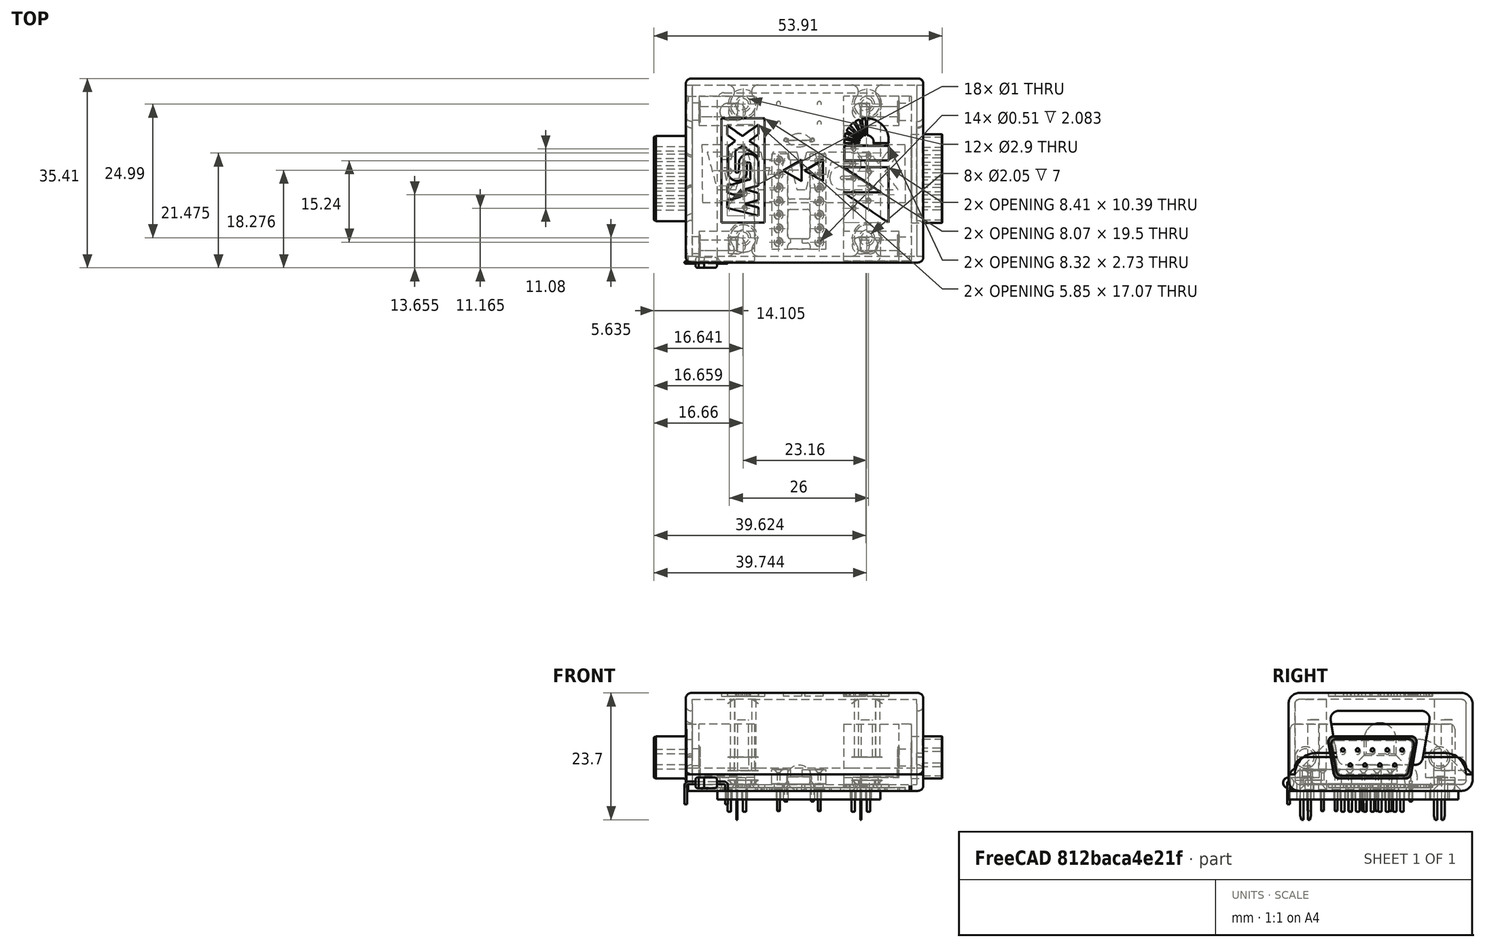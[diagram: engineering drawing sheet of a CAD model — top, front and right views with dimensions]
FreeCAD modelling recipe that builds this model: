
FCSTD DOCUMENT  (FreeCAD 0.19R)
Label: msx_mega_adapter_case
License: All rights reserved
LicenseURL: http://en.wikipedia.org/wiki/All_rights_reserved
objects: Sketcher::SketchObject×46, PartDesign::Pocket×19, PartDesign::Pad×11, Part::Feature×11, Part::Extrusion×9, Part::FeaturePython×9, App::Part×7, PartDesign::Fillet×6, PartDesign::Hole×6, PartDesign::LinearPattern×5, PartDesign::MultiTransform×3, PartDesign::Plane×3, PartDesign::Body×3, App::DocumentObjectGroup×3, Spreadsheet::Sheet×2, PartDesign::CoordinateSystem×1, App::Link×1
note: 174 computed .brp shape members not serialized (recipe doc carries the construction recipe); baked Part::Feature solids carry a one-line shape summary decoded from their .brp

FEATURE [Sketcher::SketchObject] Sketch  label="Initial sketch"
  FullyConstrained = true
  MapMode = 5
  Support = -> [XY_Plane001]
  expr: .Constraints.case_width = Spreadsheet.case_width
  expr: .Constraints.enclosure_length = Spreadsheet.case_length
  sketch-geometry (4):
    g0: LineSegment StartX=0 StartY=0 StartZ=0 EndX=44.4 EndY=0 EndZ=0
    g1: LineSegment StartX=44.4 StartY=0 StartZ=0 EndX=44.4 EndY=34.4 EndZ=0
    g2: LineSegment StartX=44.4 StartY=34.4 StartZ=0 EndX=0 EndY=34.4 EndZ=0
    g3: LineSegment StartX=0 StartY=34.4 StartZ=0 EndX=0 EndY=0 EndZ=0
  constraints (11):
    c: Coincident(g0,g1)
    c: Coincident(g1,g2)
    c: Coincident(g2,g3)
    c: Coincident(g3,g0)
    c: Horizontal(g0)
    c: Horizontal(g2)
    c: Vertical(g1)
    c: Vertical(g3)
    c: Coincident(g0,g-1)
    c: Distance(g2) = 44.4  'enclosure_length'
    c: Distance(g1) = 34.4  'case_width'
FEATURE [PartDesign::Pad] Pad  label="Initial Pad"
  Direction = (1,1,1)
  Length = 18.3
  Length2 = 100
  Profile = -> Sketch
  Type = 0
  expr: Length = Spreadsheet.case_heigth
FEATURE [Spreadsheet::Sheet] Spreadsheet
  cells = A1=Parameter description; B1=Parameter alias; C1=Value; A2=PCB - Length; B2=pcb_length; C2(pcb_length)=42; A3=PCB - Width; B3=pcb_width; C3(pcb_width)=31.6; A4=PCB - Thickness; B4=pcb_thickness; C4(pcb_thickness)=1.6; A5=PCB - Bottom clearance; B5=pcb_bottom_clearance; C5(pcb_bottom_clearance)=0.8; A6=PCB - Hole distance between connectors; B6=pcb_hole_dist_connectors; C6(pcb_hole_dist_connectors)=23.16; A7=Clearance between PCB and case; B7=clearance; C7(clearance)=0.2; A8=Connector clearance; B8=connector_clearance; C8(connector_clearance)=0.8; A9=Electronics heigth; B9=electronics_heigth; C9(electronics_heigth)=12.4; A10=Case - Wall thickness; B10=case_wall_thickness; C10(case_wall_thickness)=1.2; A11=Case - Upper clearance; B11=case_upper_clearance; C11(case_upper_clearance)=0.5; A12=Case - Top/Bottom thickness; B12=case_top_bottom_thickness; C12(case_top_bottom_thickness)=1.5; A13=Case - Length; B13=case_length; C13(case_length)==pcb_length + 2 * case_wall_thickness; A14=Case - Width; B14=case_width; C14(case_width)==pcb_width + 2 * (clearance + case_wall_thickness); A15=Case - Heigth; B15=case_heigth; C15(case_heigth)==2 * case_top_bottom_thickness + pcb_bottom_clearance + pcb_thickness + electronics_heigth + case_upper_clearance; A16=Case - External fillet; B16=case_external_fillet; C16(case_external_fillet)=2; A17=Case - Front and rear faces fillet; B17=case_front_rear_fillet; C17(case_front_rear_fillet)=1; A18=Case - DB9 hole center height; B18=case_db9_hole_center_height; C18(case_db9_hole_center_height)==case_wall_thickness + pcb_bottom_clearance + pcb_thickness + db9_screw_hole_heigth; A19=DB9 - Shield width (A); B19=db9_shield_width; C19(db9_shield_width)=30.84; A20=DB9 - Distance between screws (B); B20=db9_distance_screws; C20(db9_distance_screws)=24.99; A21=DB9 - Connector max width (C); B21=db9_connector_max_width; C21(db9_connector_max_width)=16.92; A22=DB9 - Connector max heigth; B22=db9_connector_max_heigth; C22(db9_connector_max_heigth)=8.5; A23=DB9 - Screw hole heigth; B23=db9_screw_hole_heigth; C23(db9_screw_hole_heigth)=6.3; A24=DB9 - Distance from bottom hole to front shield; B24=db9_bottom_hole_front_shield; C24(db9_bottom_hole_front_shield)==8.08 + 1.42; A25=DB9 - Connector angle; B25=db9_connector_angle; C25(db9_connector_angle)=10; A26=DB9 - Bottom distance between shield and connector; B26=db9_bottom_shield_connector; C26(db9_bottom_shield_connector)=1; A27=DB9 - Left side offset; B27=db9_left_side_offset; C27(db9_left_side_offset)=0.3; A28=DB9 - Right side offset; B28=db9_right_side_offset; C28(db9_right_side_offset)=0.65; A29=DB9 - Foot heigth; B29=db9_foot_heigth; C29(db9_foot_heigth)=2.5; A30=M3 - Non-threaded hole diameter; B30=m3_non_threaded_hole_diam; C30(m3_non_threaded_hole_diam)=2.5; A31=M3 - Non-threaded hole depth; B31=m3_non_threaded_hole_depth; C31(m3_non_threaded_hole_depth)==case_top_bottom_thickness + pcb_bottom_clearance; A32=M3 - Threaded hole depth; B32=m3_threaded_hole_depth; C32(m3_threaded_hole_depth)=7; A33=M3 - Pass-through hole; B33=m3_pass_through_hole_diam; C33(m3_pass_through_hole_diam)=3; A34=M3 - Pole radius; B34=m3_pole_radius; C34(m3_pole_radius)=2.4; A35=M3 - Castellated diameter; B35=m3_castellated_diameter; C35(m3_castellated_diameter)=5; A36=M3 - Castellated angle; B36=m3_castellated_angle; C36(m3_castellated_angle)=45; A37=Label - MSX width; B37=label_msx_width; C37(label_msx_width)=15; A38=Label - MSX heigth; B38=label_msx_heigth; C38(label_msx_heigth)=6.211; A39=Label - MSX horizontal position; B39=label_msx_hpos; C39(label_msx_hpos)==case_wall_thickness + db9_bottom_hole_front_shield; A40=Label - MSX vertical position; B40=label_msx_vpos; C40(label_msx_vpos)==case_width / 2; A41=Label - MD horizontal position; B41=label_md_hpos; C41(label_md_hpos)==case_length - (case_wall_thickness + db9_bottom_hole_front_shield); A42=Label - MD vertical position; B42=label_md_vpos; C42(label_md_vpos)==case_width / 2; A43=Cable - Stress relief diameter; B43=cable_stress_relief_diam; C43(cable_stress_relief_diam)=5.3; A44=Slice - Sides angle; B44=slice_sides_angle; C44(slice_sides_angle)=45
FEATURE [PartDesign::Fillet] Fillet  label="Case Fillet"
  Base = -> Pad [Edge9,Edge3,Edge10,Edge4]
  BaseFeature = -> Pad
  Radius = 2
  SupportTransform = false
  expr: Radius = Spreadsheet.case_external_fillet
FEATURE [PartDesign::CoordinateSystem] Local_CS_ead3
  AttacherType = Attacher::AttachEngine3D
  MapMode = 2
  Support = -> [X_Axis002]
FEATURE [Part::Feature] Pcb_ead3
  Placement = pos=(-110.3,90.8,0) rot=(0,0,1;0rad)
  shape: bbox 30.48 x 31.75 x 1.6 mm, 52 faces (baked)
FEATURE [Sketcher::SketchObject] PCB_Sketch_ead3
  FullyConstrained = false
  sketch-geometry (8):
    g0: LineSegment StartX=7.175 StartY=31.745 StartZ=0 EndX=35.115 EndY=31.745 EndZ=0
    g1: LineSegment StartX=5.905 StartY=1.265 StartZ=0 EndX=5.905 EndY=30.475 EndZ=0
    g2: LineSegment StartX=35.115 StartY=-0.005 StartZ=0 EndX=7.175 EndY=-0.005 EndZ=0
    g3: LineSegment StartX=36.385 StartY=30.475 StartZ=0 EndX=36.385 EndY=1.265 EndZ=0
    g4: ArcOfCircle CenterX=7.175 CenterY=1.265 CenterZ=0 NormalX=0 NormalY=0 NormalZ=-1 AngleXU=-1.5708 Radius=1.27 StartAngle=0 EndAngle=1.5708
    g5: ArcOfCircle CenterX=35.115 CenterY=1.265 CenterZ=0 NormalX=0 NormalY=0 NormalZ=-1 AngleXU=3.14159 Radius=1.27 StartAngle=0 EndAngle=1.5708
    g6: ArcOfCircle CenterX=7.175 CenterY=30.475 CenterZ=0 NormalX=0 NormalY=0 NormalZ=-1 AngleXU=-1.04279e-06 Radius=1.27 StartAngle=0 EndAngle=1.5708
    g7: ArcOfCircle CenterX=35.115 CenterY=30.475 CenterZ=0 NormalX=0 NormalY=0 NormalZ=-1 AngleXU=1.5708 Radius=1.27 StartAngle=0 EndAngle=1.5708
  constraints (8):
    c: Coincident(g1,g4)
    c: Coincident(g1,g6)
    c: Coincident(g2,g4)
    c: Coincident(g0,g6)
    c: Coincident(g2,g5)
    c: Coincident(g0,g7)
    c: Coincident(g3,g5)
    c: Coincident(g3,g7)
FEATURE [Part::Feature] Shape  label="J1_DSUB-9_Female_Horizontal_P2.77x2.84mm_EdgePinOffset7.70mm_Housed_
MountingHolesOffset9.12mm_00005d11216c"
  Placement = pos=(10.985,10.155,0) rot=(0,0,-1;1.5708rad)
  shape: bbox 18.74 x 30.96 x 17.98 mm, 179 faces (baked)
FEATURE [Part::Feature] Shape001  label="J2_DSUB-9_Male_Horizontal_P2.77x2.84mm_EdgePinOffset7.70mm_Housed_
MountingHolesOffset9.12mm_00005da618ed"
  Placement = pos=(31.305,10.155,0) rot=(0,0,1;1.5708rad)
  shape: bbox 18.44 x 30.96 x 17.98 mm, 181 faces (baked)
FEATURE [Part::Feature] Shape002  label="C1_C_Disc_D47mm_W25mm_P500mm_00005fced085"
  Placement = pos=(23.685,22.855,0) rot=(0,0,1;3.14159rad)
  shape: bbox 5.5 x 2.5 x 6.8 mm, 10 faces (baked)
FEATURE [Part::Feature] Shape003  label="U1_DIP_14_W762mm_Socket_00005fced0e1"
  Placement = pos=(17.335,19.045,0) rot=(0,0,1;0rad)
  shape: bbox 10.16 x 17.78 x 7.787 mm, 207 faces (baked)
FEATURE [Part::Feature] Part__Feature  label="D_DO-35_SOD27_P7.62mm_Horizontal"
  shape: bbox 8.244 x 0.5 x 4.312 mm, 7 faces (baked)
FEATURE [Part::Feature] Part__Feature001  label="D_DO-35_SOD27_P7.62mm_Horizontal001"
  shape: bbox 4 x 2.165 x 2.165 mm, 9 faces (baked)
FEATURE [App::Part] D_DO_35_SOD27_P7_62mm_Horizontal  label="D2_D_DO-35_SOD27_P7.62mm_Horizontal002_00005fced598"
  Group = -> [Part__Feature,Part__Feature001]
  Origin = -> Origin008
  Placement = pos=(24.955,26.03,0) rot=(0,0,1;3.14159rad)
FEATURE [App::Link] D2_D_DO_35_SOD27_P7_62mm_Horizontal002_00005fced598_ln_  label="D1_D_DO-35_SOD27_P7.62mm_Horizontal002_00005fcede50"
  LinkPlacement = pos=(24.955,29.713,0) rot=(0,0,1;3.14159rad)
  LinkedObject = -> D_DO_35_SOD27_P7_62mm_Horizontal
  Placement = pos=(24.955,29.713,0) rot=(0,0,1;3.14159rad)
FEATURE [App::Part] Top_ead3
  Group = -> [Shape,Shape001,Shape002,Shape003,D_DO_35_SOD27_P7_62mm_Horizontal,D2_D_DO_35_SOD27_P7_62mm_Horizontal002_00005fced598_ln_]
  Origin = -> Origin005
FEATURE [App::Part] Step_Models_ead3
  Group = -> [Top_ead3]
  Origin = -> Origin004
FEATURE [Part::Feature] pads_area006001  label="topPads_ead3"
  Placement = pos=(-110.3,90.8,0.02) rot=(0,0,1;0rad)
  shape: bbox 27.6 x 29.32 x 2e-07 mm, 42 faces, 0 solids (baked)
FEATURE [Part::Feature] Shape004001  label="topTracks_ead3"
  Placement = pos=(-110.3,90.8,0.01) rot=(0,0,1;0rad)
  shape: bbox 29.57 x 22.35 x 2e-07 mm, 11 faces, 0 solids (baked)
FEATURE [Part::Feature] pads_area006008001  label="botPads_ead3"
  Placement = pos=(-110.3,90.8,-1.62) rot=(0,0,1;0rad)
  shape: bbox 27.6 x 29.32 x 2e-07 mm, 42 faces, 0 solids (baked)
FEATURE [Part::Feature] zones_area001  label="botZones_ead3"
  Placement = pos=(-110.3,90.8,-1.61) rot=(0,0,1;0rad)
  shape: bbox 29.51 x 30.78 x 2e-07 mm, 1 faces, 0 solids (baked)
FEATURE [App::Part] Board_Geoms_ead3
  Group = -> [Pcb_ead3,PCB_Sketch_ead3,pads_area006001,Shape004001,pads_area006008001,zones_area001]
  Origin = -> Origin003
FEATURE [App::Part] Board_ead3  label="MSX Mega Adapter PCB"
  Group = -> [Local_CS_ead3,Board_Geoms_ead3,Step_Models_ead3]
  Origin = -> Origin002
  Placement = pos=(1.2,1.4,3.6) rot=(0,0,1;0rad)
  expr: .Placement.Base.x = Spreadsheet.case_wall_thickness
  expr: .Placement.Base.y = Spreadsheet.case_wall_thickness + Spreadsheet.clearance
  expr: .Placement.Base.z = Spreadsheet.case_wall_thickness + Spreadsheet.pcb_bottom_clearance + Spreadsheet.pcb_thickness
FEATURE [Sketcher::SketchObject] Sketch001  label="db9_male_hole"
  FullyConstrained = true
  MapMode = 5
  Placement = pos=(44.4,0,0) rot=(0.57735,0.57735,0.57735;2.0944rad)
  Support = -> [Fillet]
  expr: Constraints[11] = Spreadsheet.db9_connector_max_width / 2 + Spreadsheet.connector_clearance
  expr: Constraints[18] = Spreadsheet.db9_connector_max_heigth + 2 * Spreadsheet.connector_clearance
  expr: Constraints[19] = Spreadsheet.case_wall_thickness + Spreadsheet.clearance + Spreadsheet.db9_left_side_offset + Spreadsheet.db9_shield_width / 2
  expr: Constraints[28] = Spreadsheet.case_db9_hole_center_height
  sketch-geometry (12):
    g0: LineSegment StartX=9.36 StartY=14.95 StartZ=0 EndX=24.88 EndY=14.95 EndZ=0
    g1: LineSegment StartX=26.3572 StartY=13.1895 StartZ=0 EndX=25.1053 EndY=6.08953 EndZ=0
    g2: LineSegment StartX=23.6281 StartY=4.85 StartZ=0 EndX=10.6119 EndY=4.85 EndZ=0
    g3: LineSegment StartX=9.13471 StartY=6.08953 StartZ=0 EndX=7.88279 EndY=13.1895 EndZ=0
    g4: LineSegment StartX=17.12 StartY=14.95 StartZ=0 EndX=17.12 EndY=0 EndZ=0
    g5: ArcOfCircle CenterX=9.36 CenterY=13.45 CenterZ=0 NormalX=0 NormalY=0 NormalZ=1 AngleXU=0 Radius=1.5 StartAngle=1.5708 EndAngle=3.31613
    g6: ArcOfCircle CenterX=24.88 CenterY=13.45 CenterZ=0 NormalX=0 NormalY=0 NormalZ=1 AngleXU=0 Radius=1.5 StartAngle=6.10865 EndAngle=7.85398
    g7: ArcOfCircle CenterX=23.6281 CenterY=6.35 CenterZ=0 NormalX=0 NormalY=0 NormalZ=1 AngleXU=0 Radius=1.5 StartAngle=4.71239 EndAngle=6.10865
    g8: ArcOfCircle CenterX=10.6119 CenterY=6.35 CenterZ=0 NormalX=0 NormalY=0 NormalZ=1 AngleXU=0 Radius=1.5 StartAngle=3.31613 EndAngle=4.71239
    g9: LineSegment StartX=7.86 StartY=14.95 StartZ=0 EndX=7.86 EndY=4.85 EndZ=0
    g10: LineSegment StartX=26.38 StartY=14.95 StartZ=0 EndX=26.38 EndY=4.85 EndZ=0
    g11: GeomPoint X=7.86 Y=9.9 Z=0
  constraints (29):
    c: Horizontal(g0)
    c: PointOnObject(g4,g-1)
    c: Tangent(g0,g5) = 1.5708
    c: Tangent(g3,g5) = 1.5708
    c: Tangent(g0,g6) = 1.5708
    c: Tangent(g1,g6) = 1.5708
    c: Tangent(g1,g7) = 1.5708
    c: Tangent(g2,g7) = 1.5708
    c: Tangent(g2,g8) = 1.5708
    c: Tangent(g3,g8) = 1.5708
    c: Vertical(g9)
    c: Distance(g9,g4) = 9.26
    c: Vertical(g10)
    c: Tangent(g6,g10)
    c: Symmetric(g0,g0,g4)
    c: Symmetric(g2,g2,g4)
    c: Angle(g4,g3) = 0.174533
    c: Symmetric(g3,g1,g4)
    c: Distance(g2,g0) = 10.1
    c: Distance(g4,g-2) = 17.12
    c: Radius(g5) = 1.5
    c: Radius(g8) = 1.5
    c: Horizontal(g4,g9)
    c: Horizontal(g2,g10)
    c: Horizontal(g9,g2)
    c: PointOnObject(g9,g0)
    c: Symmetric(g10,g9,g4)
    c: Symmetric(g9,g9,g11)
    c: Distance(g11,g-1) = 9.9
FEATURE [PartDesign::Pocket] Pocket  label="DB9 Connector holes"
  BaseFeature = -> Fillet
  Length = 44.4
  Length2 = 100
  Profile = -> Sketch001
  Type = 0
  expr: Length = Spreadsheet.case_length
FEATURE [Sketcher::SketchObject] Sketch002  label="case_inner void"
  AttachmentOffset = pos=(0,0,1.2) rot=(0,0,1;0rad)
  ExternalGeometry = -> [Pocket]
  FullyConstrained = true
  MapMode = 5
  Placement = pos=(1.2,-3e-16,3e-16) rot=(0.57735,0.57735,0.57735;2.0944rad)
  Support = -> [YZ_Plane001]
  expr: .AttachmentOffset.Base.z = Spreadsheet.case_wall_thickness
  expr: Constraints[15] = Spreadsheet.case_wall_thickness
  expr: Constraints[16] = Spreadsheet.case_wall_thickness
  expr: Constraints[17] = Spreadsheet.case_wall_thickness
  expr: Constraints[18] = Spreadsheet.case_wall_thickness
  sketch-geometry (8):
    g0: LineSegment StartX=32.4 StartY=17.1 StartZ=0 EndX=2 EndY=17.1 EndZ=0
    g1: LineSegment StartX=1.2 StartY=16.3 StartZ=0 EndX=1.2 EndY=2 EndZ=0
    g2: LineSegment StartX=2 StartY=1.2 StartZ=0 EndX=32.4 EndY=1.2 EndZ=0
    g3: LineSegment StartX=33.2 StartY=2 StartZ=0 EndX=33.2 EndY=16.3 EndZ=0
    g4: ArcOfCircle CenterX=32.4 CenterY=16.3 CenterZ=0 NormalX=0 NormalY=0 NormalZ=1 AngleXU=0 Radius=0.8 StartAngle=3.4e-15 EndAngle=1.5708
    g5: ArcOfCircle CenterX=32.4 CenterY=2 CenterZ=0 NormalX=0 NormalY=0 NormalZ=1 AngleXU=0 Radius=0.8 StartAngle=4.71239 EndAngle=6.28319
    g6: ArcOfCircle CenterX=2 CenterY=2 CenterZ=0 NormalX=0 NormalY=0 NormalZ=1 AngleXU=0 Radius=0.8 StartAngle=3.14159 EndAngle=4.71239
    g7: ArcOfCircle CenterX=2 CenterY=16.3 CenterZ=0 NormalX=0 NormalY=0 NormalZ=1 AngleXU=0 Radius=0.8 StartAngle=1.5708 EndAngle=3.14159
  constraints (20):
    c: Tangent(g0,g4) = -1.5708
    c: Tangent(g3,g4) = -1.5708
    c: Tangent(g3,g5) = -1.5708
    c: Tangent(g2,g5) = -1.5708
    c: Tangent(g2,g6) = -1.5708
    c: Tangent(g1,g6) = -1.5708
    c: Tangent(g0,g7) = -1.5708
    c: Tangent(g1,g7) = -1.5708
    c: Horizontal(g0)
    c: Horizontal(g2)
    c: Vertical(g1)
    c: Vertical(g3)
    c: Equal(g7,g6)
    c: Equal(g6,g5)
    c: Equal(g5,g4)
    c: Distance(g0,g-3) = 1.2
    c: Distance(g3,g-5) = 1.2
    c: Distance(g1,g-9) = 1.2
    c: Distance(g2,g-7) = 1.2
    c: Vertical(g0,g-10)
FEATURE [PartDesign::Pocket] Pocket001  label="Case emptying"
  BaseFeature = -> Pocket
  Length = 42
  Length2 = 100
  Profile = -> Sketch002
  Reversed = true
  Type = 0
  expr: Length = Spreadsheet.case_length - 2 * Spreadsheet.case_wall_thickness
FEATURE [Sketcher::SketchObject] Sketch003  label="pcb_front_support_sketch"
  ExternalGeometry = -> [Pocket001]
  FullyConstrained = true
  MapMode = 5
  Placement = pos=(-3e-16,3e-16,1.2) rot=(0,0,1;0rad)
  Support = -> [Pocket001]
  expr: Constraints[10] = Spreadsheet.m3_pole_radius
  expr: Constraints[2] = Spreadsheet.db9_distance_screws / 2
  expr: Constraints[9] = Spreadsheet.m3_pass_through_hole_diam
  expr: Constraints[0] = Spreadsheet.case_wall_thickness + Spreadsheet.db9_bottom_hole_front_shield
  expr: Constraints[4] = Spreadsheet.case_wall_thickness + Spreadsheet.db9_bottom_hole_front_shield
  sketch-geometry (13):
    g0: ArcOfCircle CenterX=10.7 CenterY=4.625 CenterZ=0 NormalX=0 NormalY=0 NormalZ=1 AngleXU=0 Radius=2.4 StartAngle=5.60805 EndAngle=10.0999
    g1: LineSegment StartX=1.4e-15 StartY=17.12 StartZ=0 EndX=10.7 EndY=17.12 EndZ=0
    g2: ArcOfCircle CenterX=13.4982 CenterY=2.38462 CenterZ=0 NormalX=0 NormalY=0 NormalZ=1 AngleXU=0 Radius=1.18462 StartAngle=2.46646 EndAngle=4.71239
    g3: ArcOfCircle CenterX=7.90176 CenterY=2.38462 CenterZ=0 NormalX=0 NormalY=0 NormalZ=1 AngleXU=0 Radius=1.18462 StartAngle=4.71239 EndAngle=6.95832
    g4: Circle CenterX=10.7 CenterY=4.625 CenterZ=0 NormalX=0 NormalY=0 NormalZ=1 AngleXU=0 Radius=1.5
    g5: GeomPoint X=10.7 Y=3.125 Z=0
    g6: LineSegment StartX=7.90176 StartY=1.2 StartZ=0 EndX=13.4982 EndY=1.2 EndZ=0
    g7: GeomPoint X=10.7 Y=1.2 Z=0
    g8: LineSegment StartX=7.8249 StartY=33.2 StartZ=0 EndX=13.5751 EndY=33.2 EndZ=0
    g9: ArcOfCircle CenterX=7.8249 CenterY=31.9169 CenterZ=0 NormalX=0 NormalY=0 NormalZ=1 AngleXU=0 Radius=1.28308 StartAngle=5.60805 EndAngle=7.85398
    g10: ArcOfCircle CenterX=10.7 CenterY=29.615 CenterZ=0 NormalX=0 NormalY=0 NormalZ=1 AngleXU=0 Radius=2.4 StartAngle=2.46646 EndAngle=6.95832
    g11: ArcOfCircle CenterX=13.5751 CenterY=31.9169 CenterZ=0 NormalX=0 NormalY=0 NormalZ=1 AngleXU=0 Radius=1.28308 StartAngle=1.5708 EndAngle=3.81672
    g12: GeomPoint X=10.7 Y=33.2 Z=0
  constraints (31):
    c: Distance(g0,g-2) = 10.7
    c: Horizontal(g1)
    c: Distance(g0,g1) = 12.495
    c: Symmetric(g-3,g-3,g1)
    c: Distance(g1) = 10.7
    c: Equal(g3,g2)
    c: Tangent(g0,g2) = 1.5708
    c: Tangent(g0,g3) = 1.5708
    c: Coincident(g4,g0)
    c: Diameter(g4) = 3
    c: Radius(g0) = 2.4
    c: PointOnObject(g5,g4)
    c: Vertical(g5,g0)
    c: Horizontal(g5,g0)
    c: Horizontal(g0,g0)
    c: Coincident(g6,g3)
    c: Horizontal(g6)
    c: Symmetric(g3,g2,g7)
    c: PointOnObject(g3,g-4)
    c: Tangent(g6,g2) = -1.5708
    c: Equal(g9,g11)
    c: Tangent(g10,g11) = 1.5708
    c: Tangent(g10,g9) = 1.5708
    c: Coincident(g8,g9)
    c: Horizontal(g8)
    c: Tangent(g8,g11) = 1.5708
    c: Symmetric(g10,g0,g1)
    c: Symmetric(g0,g9,g1)
    c: PointOnObject(g8,g-5)
    c: Symmetric(g8,g8,g12)
    c: Vertical(g12,g10)
FEATURE [PartDesign::Pad] Pad001  label="PCB front support"
  BaseFeature = -> Pocket001
  Direction = (1,1,1)
  Length = 0.8
  Length2 = 100
  Profile = -> Sketch003
  Type = 2
  expr: Length = Spreadsheet.pcb_bottom_clearance
FEATURE [Sketcher::SketchObject] Sketch005  label="Bottom hole sketch"
  ExternalGeometry = -> [Pad001]
  FullyConstrained = true
  MapMode = 5
  Placement = pos=(0,0,0) rot=(1,0,0;3.14159rad)
  Support = -> [Pad001]
  expr: Constraints[0] = Spreadsheet.m3_pass_through_hole_diam
  sketch-geometry (2):
    g0: Circle CenterX=10.7 CenterY=-4.625 CenterZ=0 NormalX=0 NormalY=0 NormalZ=1 AngleXU=0 Radius=1.5
    g1: Circle CenterX=10.7 CenterY=-29.615 CenterZ=0 NormalX=0 NormalY=0 NormalZ=1 AngleXU=0 Radius=1.5
  constraints (4):
    c: Diameter(g0) = 3
    c: Coincident(g0,g-3)
    c: Coincident(g1,g-4)
    c: Equal(g1,g0)
FEATURE [PartDesign::LinearPattern] LinearPattern  label="Supports LinearPattern"
  Direction = -> X_Axis001
  Length = 23.16
  Occurrences = 2
  expr: Length = Spreadsheet.pcb_hole_dist_connectors
FEATURE [PartDesign::Hole] Hole  label="Bottom hole"
  BaseFeature = -> Pad001
  Depth = 2
  DepthType = 0
  Diameter = 2.9
  DrillForDepth = false
  DrillPoint = 0
  DrillPointAngle = 118
  HoleCutCountersinkAngle = 90
  HoleCutCustomValues = false
  HoleCutDepth = 1.2
  HoleCutDiameter = 5.5
  HoleCutType = 2
  ModelActualThread = false
  Profile = -> Sketch005
  Tapered = false
  TaperedAngle = 90
  ThreadAngle = 60
  ThreadClass = 0
  ThreadCutOffInner = 0.0487139
  ThreadCutOffOuter = 0.0974279
  ThreadDirection = 0
  ThreadFit = 0
  ThreadPitch = 0.45
  ThreadSize = 8
  ThreadType = 1
  Threaded = false
  expr: HoleCutDepth = Spreadsheet.case_wall_thickness
  expr: Depth = Spreadsheet.case_wall_thickness + Spreadsheet.pcb_bottom_clearance
FEATURE [Sketcher::SketchObject] Sketch006  label="Middle cut sketch"
  ExternalGeometry = -> [Hole,Sketch003]
  FullyConstrained = true
  MapMode = 5
  Placement = pos=(0,0,2) rot=(1,0,0;3.14159rad)
  Support = -> [Hole]
  sketch-geometry (8):
    g0: ArcOfCircle CenterX=10.7 CenterY=-4.625 CenterZ=0 NormalX=0 NormalY=0 NormalZ=1 AngleXU=0 Radius=2.4 StartAngle=3.25303 EndAngle=6.17175
    g1: LineSegment StartX=8.31489 StartY=-4.8919 StartZ=0 EndX=7.90176 EndY=-1.2 EndZ=0
    g2: LineSegment StartX=13.0851 StartY=-4.8919 StartZ=0 EndX=13.4982 EndY=-1.2 EndZ=0
    g3: ArcOfCircle CenterX=10.7 CenterY=-29.615 CenterZ=0 NormalX=0 NormalY=0 NormalZ=1 AngleXU=0 Radius=2.4 StartAngle=0.126458 EndAngle=3.01514
    g4: LineSegment StartX=8.31916 StartY=-29.3123 StartZ=0 EndX=7.8249 EndY=-33.2 EndZ=0
    g5: LineSegment StartX=13.0808 StartY=-29.3123 StartZ=0 EndX=13.5751 EndY=-33.2 EndZ=0
    g6: LineSegment StartX=7.8249 StartY=-33.2 StartZ=0 EndX=13.5751 EndY=-33.2 EndZ=0
    g7: LineSegment StartX=7.90176 StartY=-1.2 StartZ=0 EndX=13.4982 EndY=-1.2 EndZ=0
  constraints (16):
    c: Tangent(g0,g2) = -1.5708
    c: Tangent(g1,g0) = 1.5708
    c: Coincident(g5,g6)
    c: Coincident(g4,g6)
    c: Coincident(g2,g7)
    c: Coincident(g1,g7)
    c: Coincident(g3,g-5)
    c: PointOnObject(g3,g-5)
    c: Coincident(g0,g-6)
    c: Coincident(g1,g-8)
    c: Coincident(g2,g-8)
    c: PointOnObject(g0,g-6)
    c: Coincident(g4,g-7)
    c: Tangent(g3,g4) = -1.5708
    c: Tangent(g5,g3) = 1.5708
    c: Coincident(g5,g-7)
FEATURE [PartDesign::Pocket] Pocket002  label="Middle cut for pcb and DB9 foot"
  BaseFeature = -> Hole
  Length = 4.3
  Length2 = 100
  Profile = -> Sketch006
  Type = 0
  expr: Length = Spreadsheet.db9_foot_heigth + Spreadsheet.pcb_thickness + Spreadsheet.clearance
FEATURE [Sketcher::SketchObject] Sketch007  label="M3 threaded sketch"
  ExternalGeometry = -> [Pocket002]
  FullyConstrained = true
  MapMode = 5
  Placement = pos=(0,0,6.3) rot=(1,0,0;3.14159rad)
  Support = -> [Pocket002]
  sketch-geometry (3):
    g0: Circle CenterX=10.7 CenterY=-4.625 CenterZ=0 NormalX=0 NormalY=0 NormalZ=1 AngleXU=0 Radius=0.5
    g1: LineSegment StartX=0 StartY=-17.12 StartZ=0 EndX=10.7 EndY=-17.12 EndZ=0
    g2: Circle CenterX=10.7 CenterY=-29.615 CenterZ=0 NormalX=0 NormalY=0 NormalZ=1 AngleXU=0 Radius=0.5
  constraints (7):
    c: Diameter(g0) = 1
    c: Horizontal(g1)
    c: Symmetric(g-3,g-3,g1)
    c: Vertical(g1,g0)
    c: Equal(g0,g2)
    c: Symmetric(g0,g2,g1)
    c: Coincident(g2,g-4)
FEATURE [PartDesign::Hole] Hole001  label="M3 threaded hole"
  BaseFeature = -> Pocket002
  Depth = 7
  DepthType = 0
  Diameter = 2.05
  DrillForDepth = false
  DrillPoint = 0
  DrillPointAngle = 118
  HoleCutCountersinkAngle = 90
  HoleCutCustomValues = false
  HoleCutDepth = 0
  HoleCutDiameter = 6.1
  HoleCutType = 0
  ModelActualThread = false
  Profile = -> Sketch007
  Tapered = false
  TaperedAngle = 90
  ThreadAngle = 60
  ThreadClass = 0
  ThreadCutOffInner = 0.0487139
  ThreadCutOffOuter = 0.0974279
  ThreadDirection = 0
  ThreadFit = 0
  ThreadPitch = 0.45
  ThreadSize = 8
  ThreadType = 1
  Threaded = true
  expr: Depth = Spreadsheet.m3_threaded_hole_depth
FEATURE [PartDesign::MultiTransform] MultiTransform  label="Supports replication"
  BaseFeature = -> Hole001
  Originals = -> [Pad001,Hole,Pocket002,Hole001]
  Transformations = -> [LinearPattern]
FEATURE [Sketcher::SketchObject] Sketch008  label="Split wire left"
  ExternalGeometry = -> [MultiTransform]
  FullyConstrained = true
  MapMode = 5
  Placement = pos=(0,0,0) rot=(0.57735,-0.57735,-0.57735;2.0944rad)
  Support = -> [MultiTransform]
  expr: Constraints[11] = Spreadsheet.case_external_fillet
  expr: Constraints[5] = Spreadsheet.case_top_bottom_thickness + Spreadsheet.pcb_bottom_clearance + Spreadsheet.pcb_thickness / 2
  expr: Constraints[14] = Spreadsheet.case_wall_thickness
  sketch-geometry (5):
    g0: LineSegment StartX=-33.2 StartY=4.3 StartZ=0 EndX=-34.4 EndY=3.1 EndZ=0
    g1: LineSegment StartX=-1.2 StartY=4.3 StartZ=0 EndX=0 EndY=3.1 EndZ=0
    g2: LineSegment StartX=-31.2 StartY=6.3 StartZ=0 EndX=-3.2 EndY=6.3 EndZ=0
    g3: ArcOfCircle CenterX=-31.2 CenterY=4.3 CenterZ=0 NormalX=0 NormalY=0 NormalZ=1 AngleXU=0 Radius=2 StartAngle=1.5708 EndAngle=3.14159
    g4: ArcOfCircle CenterX=-3.2 CenterY=4.3 CenterZ=0 NormalX=0 NormalY=0 NormalZ=1 AngleXU=0 Radius=2 StartAngle=0 EndAngle=1.5708
  constraints (16):
    c: PointOnObject(g0,g-3)
    c: Angle(g0,g-3) = 0.785398
    c: PointOnObject(g1,g-2)
    c: Horizontal(g0,g1)
    c: Horizontal(g1,g0)
    c: Distance(g-1,g1) = 3.1
    c: Horizontal(g2)
    c: Equal(g1,g0)
    c: Tangent(g2,g3) = 1.5708
    c: Tangent(g2,g4) = 1.5708
    c: Equal(g3,g4)
    c: Radius(g3) = 2
    c: Coincident(g1,g4)
    c: Coincident(g0,g3)
    c: Distance(g0,g-3) = 1.2
    c: Horizontal(g3,g0)
FEATURE [Sketcher::SketchObject] Sketch010  label="Split wire right"
  ExternalGeometry = -> [MultiTransform]
  FullyConstrained = true
  MapMode = 5
  Placement = pos=(44.4,0,0) rot=(0.57735,0.57735,0.57735;2.0944rad)
  Support = -> [MultiTransform]
  expr: Constraints[11] = Spreadsheet.case_external_fillet
  expr: Constraints[4] = Sketch008.Constraints[5]
  expr: Constraints[14] = Spreadsheet.case_wall_thickness
  sketch-geometry (5):
    g0: LineSegment StartX=33.2 StartY=4.3 StartZ=0 EndX=34.4 EndY=3.1 EndZ=0
    g1: LineSegment StartX=1.2 StartY=4.3 StartZ=0 EndX=0 EndY=3.1 EndZ=0
    g2: LineSegment StartX=31.2 StartY=6.3 StartZ=0 EndX=3.2 EndY=6.3 EndZ=0
    g3: ArcOfCircle CenterX=3.2 CenterY=4.3 CenterZ=0 NormalX=0 NormalY=0 NormalZ=1 AngleXU=0 Radius=2 StartAngle=1.5708 EndAngle=3.14159
    g4: ArcOfCircle CenterX=31.2 CenterY=4.3 CenterZ=0 NormalX=0 NormalY=0 NormalZ=1 AngleXU=0 Radius=2 StartAngle=0 EndAngle=1.5708
  constraints (16):
    c: PointOnObject(g0,g-3)
    c: PointOnObject(g1,g-2)
    c: Horizontal(g0,g1)
    c: Horizontal(g1,g0)
    c: Distance(g-1,g1) = 3.1
    c: Horizontal(g2)
    c: Equal(g1,g0)
    c: Angle(g-3,g0) = 0.785398
    c: Tangent(g2,g3) = -1.5708
    c: Tangent(g2,g4) = -1.5708
    c: Equal(g3,g4)
    c: Radius(g3) = 2
    c: Coincident(g1,g3)
    c: Coincident(g4,g0)
    c: Distance(g0,g-3) = 1.2
    c: Horizontal(g1,g3)
FEATURE [Sketcher::SketchObject] Sketch011  label="Split wire sides"
  ExternalGeometry = -> [Sketch008]
  FullyConstrained = true
  MapMode = 5
  Placement = pos=(0,0,0) rot=(0.57735,-0.57735,-0.57735;2.0944rad)
  Support = -> [MultiTransform]
  sketch-geometry (2):
    g0: LineSegment StartX=-34.4 StartY=3.1 StartZ=0 EndX=-33.2 EndY=4.3 EndZ=0
    g1: LineSegment StartX=0 StartY=3.1 StartZ=0 EndX=-1.2 EndY=4.3 EndZ=0
  constraints (4):
    c: Coincident(g0,g-3)
    c: Coincident(g0,g-4)
    c: Coincident(g1,g-6)
    c: Coincident(g1,g-5)
FEATURE [Part::Extrusion] Extrude  label="Split plane left"
  Base = -> Sketch008
  Dir = (-1,0,0)
  DirMode = 2
  FaceMakerClass = Part::FaceMakerBullseye
  LengthFwd = 1.2
  LengthRev = 0
  Reversed = true
  Solid = false
  Symmetric = false
  expr: LengthFwd = Spreadsheet.case_wall_thickness
FEATURE [Part::Extrusion] Extrude001  label="Split plane sides"
  Base = -> Sketch011
  Dir = (-1,0,0)
  DirMode = 2
  FaceMakerClass = Part::FaceMakerBullseye
  LengthFwd = 44.4
  LengthRev = 0
  Reversed = true
  Solid = false
  Symmetric = false
  expr: LengthFwd = Spreadsheet.case_length
FEATURE [Part::Extrusion] Extrude002  label="Split plane right"
  Base = -> Sketch010
  Dir = (1,0,0)
  DirMode = 2
  FaceMakerClass = Part::FaceMakerBullseye
  LengthFwd = 1.2
  LengthRev = 0
  Reversed = true
  Solid = false
  Symmetric = false
FEATURE [PartDesign::Plane] DatumPlane  label="Top Plane"
  AttachmentOffset = pos=(0,0,18.3) rot=(0,0,1;0rad)
  Length = 60
  MapMode = 5
  Placement = pos=(0,0,18.3) rot=(0,0,1;0rad)
  ResizeMode = 0
  Support = -> [XY_Plane001]
  Width = 60
  expr: .AttachmentOffset.Base.z = Spreadsheet.case_heigth
FEATURE [Sketcher::SketchObject] Sketch015  label="Arrows logo"
  FullyConstrained = true
  MapMode = 5
  Placement = pos=(0,0,18.3) rot=(0,0,1;0rad)
  Support = -> [DatumPlane]
  expr: Constraints[16] = Spreadsheet.case_length / 2
  expr: Constraints[15] = Spreadsheet.case_width / 2
  sketch-geometry (6):
    g0: LineSegment StartX=21.6641 StartY=19.2 StartZ=0 EndX=18.2 EndY=17.2 EndZ=0
    g1: LineSegment StartX=18.2 StartY=17.2 StartZ=0 EndX=21.6641 EndY=15.2 EndZ=0
    g2: LineSegment StartX=21.6641 StartY=15.2 StartZ=0 EndX=21.6641 EndY=19.2 EndZ=0
    g3: LineSegment StartX=25.6641 StartY=19.2 StartZ=0 EndX=22.2 EndY=17.2 EndZ=0
    g4: LineSegment StartX=22.2 StartY=17.2 StartZ=0 EndX=25.6641 EndY=15.2 EndZ=0
    g5: LineSegment StartX=25.6641 StartY=15.2 StartZ=0 EndX=25.6641 EndY=19.2 EndZ=0
  constraints (18):
    c: Coincident(g1,g0)
    c: Coincident(g2,g1)
    c: Coincident(g2,g0)
    c: Vertical(g2)
    c: Angle(g2,g1) = 1.0472
    c: Angle(g1,g0) = 1.0472
    c: Coincident(g4,g3)
    c: Coincident(g5,g4)
    c: Coincident(g5,g3)
    c: Vertical(g5)
    c: Angle(g5,g4) = 1.0472
    c: Angle(g4,g3) = 1.0472
    c: Horizontal(g1,g4)
    c: Horizontal(g3,g0)
    c: Distance(g0,g5) = 4
    c: Distance(g0,g-1) = 17.2
    c: Distance(g3,g-2) = 22.2
    c: Distance(g5) = 4
FEATURE [Sketcher::SketchObject] Sketch016  label="MSX Logo"
  AttachmentOffset = pos=(10.7,17.2,0) rot=(0,0,1;1.5708rad)
  FullyConstrained = false
  MapMode = 5
  Placement = pos=(10.7,17.2,18.3) rot=(0,0,1;1.5708rad)
  Support = -> [DatumPlane]
  expr: .AttachmentOffset.Base.x = Spreadsheet.label_msx_hpos
  expr: .AttachmentOffset.Base.y = Spreadsheet.label_msx_vpos
  sketch-geometry (39):
    g0: BSplineCurve PolesCount=2 KnotsCount=2 Degree=1 IsPeriodic=0
    g1: BSplineCurve PolesCount=2 KnotsCount=2 Degree=1 IsPeriodic=0
    g2: BSplineCurve PolesCount=2 KnotsCount=2 Degree=1 IsPeriodic=0
    g3: BSplineCurve PolesCount=2 KnotsCount=2 Degree=1 IsPeriodic=0
    g4: BSplineCurve PolesCount=2 KnotsCount=2 Degree=1 IsPeriodic=0
    g5: BSplineCurve PolesCount=2 KnotsCount=2 Degree=1 IsPeriodic=0
    g6: BSplineCurve PolesCount=2 KnotsCount=2 Degree=1 IsPeriodic=0
    g7: BSplineCurve PolesCount=2 KnotsCount=2 Degree=1 IsPeriodic=0
    g8: BSplineCurve PolesCount=2 KnotsCount=2 Degree=1 IsPeriodic=0
    g9: BSplineCurve PolesCount=2 KnotsCount=2 Degree=1 IsPeriodic=0
    g10: BSplineCurve PolesCount=4 KnotsCount=2 Degree=3 IsPeriodic=0
    g11: BSplineCurve PolesCount=2 KnotsCount=2 Degree=1 IsPeriodic=0
    g12: BSplineCurve PolesCount=4 KnotsCount=2 Degree=3 IsPeriodic=0
    g13: BSplineCurve PolesCount=4 KnotsCount=2 Degree=3 IsPeriodic=0
    g14: BSplineCurve PolesCount=2 KnotsCount=2 Degree=1 IsPeriodic=0
    g15: BSplineCurve PolesCount=2 KnotsCount=2 Degree=1 IsPeriodic=0
    g16: BSplineCurve PolesCount=2 KnotsCount=2 Degree=1 IsPeriodic=0
    g17: BSplineCurve PolesCount=2 KnotsCount=2 Degree=1 IsPeriodic=0
    g18: BSplineCurve PolesCount=2 KnotsCount=2 Degree=1 IsPeriodic=0
    g19: BSplineCurve PolesCount=2 KnotsCount=2 Degree=1 IsPeriodic=0
    g20: BSplineCurve PolesCount=2 KnotsCount=2 Degree=1 IsPeriodic=0
    g21: BSplineCurve PolesCount=2 KnotsCount=2 Degree=1 IsPeriodic=0
    g22: BSplineCurve PolesCount=2 KnotsCount=2 Degree=1 IsPeriodic=0
    g23: BSplineCurve PolesCount=2 KnotsCount=2 Degree=1 IsPeriodic=0
    g24: BSplineCurve PolesCount=2 KnotsCount=2 Degree=1 IsPeriodic=0
    g25: BSplineCurve PolesCount=2 KnotsCount=2 Degree=1 IsPeriodic=0
    g26: BSplineCurve PolesCount=2 KnotsCount=2 Degree=1 IsPeriodic=0
    g27: BSplineCurve PolesCount=4 KnotsCount=2 Degree=3 IsPeriodic=0
    g28: BSplineCurve PolesCount=2 KnotsCount=2 Degree=1 IsPeriodic=0
    g29: BSplineCurve PolesCount=4 KnotsCount=2 Degree=3 IsPeriodic=0
    g30: BSplineCurve PolesCount=4 KnotsCount=2 Degree=3 IsPeriodic=0
    g31: BSplineCurve PolesCount=2 KnotsCount=2 Degree=1 IsPeriodic=0
    g32: BSplineCurve PolesCount=2 KnotsCount=2 Degree=1 IsPeriodic=0
    g33: BSplineCurve PolesCount=2 KnotsCount=2 Degree=1 IsPeriodic=0
    g34: BSplineCurve PolesCount=2 KnotsCount=2 Degree=1 IsPeriodic=0
    g35: BSplineCurve PolesCount=2 KnotsCount=2 Degree=1 IsPeriodic=0
    g36: BSplineCurve PolesCount=2 KnotsCount=2 Degree=1 IsPeriodic=0
    g37: BSplineCurve PolesCount=2 KnotsCount=2 Degree=1 IsPeriodic=0
    g38: BSplineCurve PolesCount=2 KnotsCount=2 Degree=1 IsPeriodic=0
  constraints (39):
    c: Coincident(g0,g1)
    c: Coincident(g1,g2)
    c: Coincident(g2,g3)
    c: Coincident(g3,g0)
    c: Coincident(g4,g5)
    c: Coincident(g5,g6)
    c: Coincident(g6,g7)
    c: Coincident(g7,g8)
    c: Coincident(g8,g9)
    c: Coincident(g9,g10)
    c: Coincident(g10,g11)
    c: Coincident(g11,g12)
    c: Coincident(g12,g13)
    c: Coincident(g13,g14)
    c: Coincident(g14,g15)
    c: Coincident(g15,g16)
    c: Coincident(g16,g17)
    c: Coincident(g17,g18)
    c: Coincident(g18,g19)
    c: Coincident(g19,g20)
    c: Coincident(g20,g21)
    c: Coincident(g21,g22)
    c: Coincident(g22,g23)
    c: Coincident(g23,g24)
    c: Coincident(g24,g25)
    c: Coincident(g25,g26)
    c: Coincident(g26,g27)
    c: Coincident(g27,g28)
    c: Coincident(g28,g29)
    c: Coincident(g29,g30)
    c: Coincident(g30,g31)
    c: Coincident(g31,g32)
    c: Coincident(g32,g33)
    c: Coincident(g33,g34)
    c: Coincident(g34,g35)
    c: Coincident(g35,g36)
    c: Coincident(g36,g37)
    c: Coincident(g37,g38)
    c: Coincident(g38,g4)
FEATURE [PartDesign::Pocket] Pocket003  label="MSX Logo pocket"
  BaseFeature = -> MultiTransform
  Length = 0.6
  Length2 = 100
  Profile = -> Sketch016
  Type = 0
  expr: Length = Spreadsheet.case_wall_thickness / 2
FEATURE [PartDesign::Pocket] Pocket004  label="Arrows Logo pocket"
  BaseFeature = -> Pocket003
  Length = 0.6
  Length2 = 100
  Profile = -> Sketch015
  Type = 0
  expr: Length = Spreadsheet.case_wall_thickness / 2
FEATURE [Sketcher::SketchObject] Sketch017  label="MD Logo"
  AttachmentOffset = pos=(33.7,17.2,0) rot=(0,0,1;1.5708rad)
  FullyConstrained = false
  MapMode = 5
  Placement = pos=(33.7,17.2,18.3) rot=(0,0,1;1.5708rad)
  Support = -> [Pocket004,DatumPlane]
  expr: .AttachmentOffset.Base.x = Spreadsheet.label_md_hpos
  expr: .AttachmentOffset.Base.y = Spreadsheet.label_md_vpos
  sketch-geometry (50):
    g0: BSplineCurve PolesCount=2 KnotsCount=2 Degree=1 IsPeriodic=0
    g1: BSplineCurve PolesCount=2 KnotsCount=2 Degree=1 IsPeriodic=0
    g2: BSplineCurve PolesCount=2 KnotsCount=2 Degree=1 IsPeriodic=0
    g3: BSplineCurve PolesCount=2 KnotsCount=2 Degree=1 IsPeriodic=0
    g4: BSplineCurve PolesCount=2 KnotsCount=2 Degree=1 IsPeriodic=0
    g5: BSplineCurve PolesCount=2 KnotsCount=2 Degree=1 IsPeriodic=0
    g6: BSplineCurve PolesCount=2 KnotsCount=2 Degree=1 IsPeriodic=0
    g7: BSplineCurve PolesCount=2 KnotsCount=2 Degree=1 IsPeriodic=0
    g8: BSplineCurve PolesCount=2 KnotsCount=2 Degree=1 IsPeriodic=0
    g9: BSplineCurve PolesCount=2 KnotsCount=2 Degree=1 IsPeriodic=0
    g10: BSplineCurve PolesCount=2 KnotsCount=2 Degree=1 IsPeriodic=0
    g11: BSplineCurve PolesCount=2 KnotsCount=2 Degree=1 IsPeriodic=0
    g12: BSplineCurve PolesCount=4 KnotsCount=2 Degree=3 IsPeriodic=0
    g13: BSplineCurve PolesCount=2 KnotsCount=2 Degree=1 IsPeriodic=0
    g14: BSplineCurve PolesCount=4 KnotsCount=2 Degree=3 IsPeriodic=0
    g15: BSplineCurve PolesCount=2 KnotsCount=2 Degree=1 IsPeriodic=0
    g16: BSplineCurve PolesCount=4 KnotsCount=2 Degree=3 IsPeriodic=0
    g17: BSplineCurve PolesCount=4 KnotsCount=2 Degree=3 IsPeriodic=0
    g18: BSplineCurve PolesCount=2 KnotsCount=2 Degree=1 IsPeriodic=0
    g19: BSplineCurve PolesCount=2 KnotsCount=2 Degree=1 IsPeriodic=0
    g20: BSplineCurve PolesCount=4 KnotsCount=2 Degree=3 IsPeriodic=0
    g21: BSplineCurve PolesCount=2 KnotsCount=2 Degree=1 IsPeriodic=0
    g22: BSplineCurve PolesCount=4 KnotsCount=2 Degree=3 IsPeriodic=0
    g23: BSplineCurve PolesCount=2 KnotsCount=2 Degree=1 IsPeriodic=0
    g24: BSplineCurve PolesCount=4 KnotsCount=2 Degree=3 IsPeriodic=0
    g25: BSplineCurve PolesCount=2 KnotsCount=2 Degree=1 IsPeriodic=0
    g26: BSplineCurve PolesCount=4 KnotsCount=2 Degree=3 IsPeriodic=0
    g27: BSplineCurve PolesCount=2 KnotsCount=2 Degree=1 IsPeriodic=0
    g28: BSplineCurve PolesCount=4 KnotsCount=2 Degree=3 IsPeriodic=0
    g29: BSplineCurve PolesCount=2 KnotsCount=2 Degree=1 IsPeriodic=0
    g30: BSplineCurve PolesCount=4 KnotsCount=2 Degree=3 IsPeriodic=0
    g31: BSplineCurve PolesCount=2 KnotsCount=2 Degree=1 IsPeriodic=0
    g32: BSplineCurve PolesCount=2 KnotsCount=2 Degree=1 IsPeriodic=0
    g33: BSplineCurve PolesCount=4 KnotsCount=2 Degree=3 IsPeriodic=0
    g34: BSplineCurve PolesCount=2 KnotsCount=2 Degree=1 IsPeriodic=0
    g35: BSplineCurve PolesCount=4 KnotsCount=2 Degree=3 IsPeriodic=0
    g36: BSplineCurve PolesCount=2 KnotsCount=2 Degree=1 IsPeriodic=0
    g37: BSplineCurve PolesCount=2 KnotsCount=2 Degree=1 IsPeriodic=0
    g38: BSplineCurve PolesCount=4 KnotsCount=2 Degree=3 IsPeriodic=0
    g39: BSplineCurve PolesCount=2 KnotsCount=2 Degree=1 IsPeriodic=0
    g40: BSplineCurve PolesCount=4 KnotsCount=2 Degree=3 IsPeriodic=0
    g41: BSplineCurve PolesCount=2 KnotsCount=2 Degree=1 IsPeriodic=0
    g42: BSplineCurve PolesCount=4 KnotsCount=2 Degree=3 IsPeriodic=0
    g43: BSplineCurve PolesCount=4 KnotsCount=2 Degree=3 IsPeriodic=0
    g44: BSplineCurve PolesCount=2 KnotsCount=2 Degree=1 IsPeriodic=0
    g45: BSplineCurve PolesCount=4 KnotsCount=2 Degree=3 IsPeriodic=0
    g46: BSplineCurve PolesCount=2 KnotsCount=2 Degree=1 IsPeriodic=0
    g47: BSplineCurve PolesCount=4 KnotsCount=2 Degree=3 IsPeriodic=0
    g48: BSplineCurve PolesCount=4 KnotsCount=2 Degree=3 IsPeriodic=0
    g49: BSplineCurve PolesCount=2 KnotsCount=2 Degree=1 IsPeriodic=0
  constraints (50):
    c: Coincident(g0,g1)
    c: Coincident(g1,g2)
    c: Coincident(g2,g3)
    c: Coincident(g3,g4)
    c: Coincident(g4,g5)
    c: Coincident(g5,g6)
    c: Coincident(g6,g0)
    c: Coincident(g7,g8)
    c: Coincident(g8,g9)
    c: Coincident(g9,g10)
    c: Coincident(g10,g7)
    c: Coincident(g11,g12)
    c: Coincident(g12,g13)
    c: Coincident(g13,g14)
    c: Coincident(g14,g15)
    c: Coincident(g15,g16)
    c: Coincident(g16,g17)
    c: Coincident(g17,g18)
    c: Coincident(g18,g11)
    c: Coincident(g19,g20)
    c: Coincident(g20,g21)
    c: Coincident(g21,g22)
    c: Coincident(g22,g19)
    c: Coincident(g23,g24)
    c: Coincident(g24,g25)
    c: Coincident(g25,g26)
    c: Coincident(g26,g23)
    c: Coincident(g27,g28)
    c: Coincident(g28,g29)
    c: Coincident(g29,g30)
    c: Coincident(g30,g31)
    c: Coincident(g31,g27)
    c: Coincident(g32,g33)
    c: Coincident(g33,g34)
    c: Coincident(g34,g35)
    c: Coincident(g35,g36)
    c: Coincident(g36,g32)
    c: Coincident(g37,g38)
    c: Coincident(g38,g39)
    c: Coincident(g39,g40)
    c: Coincident(g40,g41)
    c: Coincident(g41,g37)
    c: Coincident(g42,g43)
    c: Coincident(g43,g44)
    c: Coincident(g44,g45)
    c: Coincident(g45,g46)
    c: Coincident(g46,g47)
    c: Coincident(g47,g48)
    c: Coincident(g48,g49)
    c: Coincident(g49,g42)
FEATURE [PartDesign::Pocket] Pocket005  label="MD Logo pocket"
  BaseFeature = -> Pocket004
  Length = 0.6
  Length2 = 100
  Profile = -> Sketch017
  Type = 0
  expr: Length = Spreadsheet.case_wall_thickness / 2
FEATURE [PartDesign::LinearPattern] LinearPattern001
  BaseFeature = -> Pocket005
  Direction = -> Sketch016 [N_Axis]
  Length = 17.1
  Occurrences = 2
  Originals = -> [Pocket003,Pocket004,Pocket005]
  Reversed = true
  expr: Length = Spreadsheet.case_heigth - Spreadsheet.case_wall_thickness
FEATURE [PartDesign::Fillet] Fillet001  label="Fillet last operation"
  Base = -> LinearPattern001 [Face5,Face2]
  BaseFeature = -> LinearPattern001
  Radius = 1
  SupportTransform = false
  expr: Radius = Spreadsheet.case_front_rear_fillet
FEATURE [PartDesign::Body] Body  label="case"
  Group = -> [DatumPlane,Sketch,Pad,Fillet,Sketch001,Pocket,Sketch002,Pocket001,Sketch003,Pad001,Sketch005,Hole,Pocket002,Hole001,Sketch007,Sketch006,MultiTransform,Pocket003,LinearPattern,Sketch016,Pocket004,Pocket005,Sketch015,Sketch017,LinearPattern001,Fillet001,Sketch008,Sketch011,Sketch010]
  Origin = -> Origin001
  Tip = -> Fillet001
FEATURE [App::Part] Part  label="MSX Mega Adapter Case"
  Group = -> [Body]
  Origin = -> Origin
FEATURE [Part::FeaturePython] Slice  # WARN: FeaturePython — macro-defined, semantics opaque (R4)
  Base = -> Body
  Mode = 1
  Tolerance = 0
  Tools = -> [Extrude,Extrude001,Extrude002]
FEATURE [Part::FeaturePython] Slice_child0  label="Bottom"  # WARN: FeaturePython — macro-defined, semantics opaque (R4)
  Base = -> Slice
  FilterType = 1
  Invert = false
  OverrideMaxVal = 0
  WindowFrom = 80
  WindowTo = 100
  items = 0
FEATURE [Part::FeaturePython] Slice_child1  label="Top"  # WARN: FeaturePython — macro-defined, semantics opaque (R4)
  Base = -> Slice
  FilterType = 1
  Invert = false
  OverrideMaxVal = 0
  WindowFrom = 80
  WindowTo = 100
  items = 1
FEATURE [App::DocumentObjectGroup] GrExplode_Slice  label="MSX-Mega Adapter Slice"
  Group = -> [Slice_child0,Slice_child1]
FEATURE [Sketcher::SketchObject] Sketch018  label="Initial sketch001"
  FullyConstrained = true
  MapMode = 5
  Support = -> [XY_Plane010]
  expr: .Constraints.enclosure_length = Spreadsheet.case_length
  expr: .Constraints.case_width = Spreadsheet.case_width
  sketch-geometry (4):
    g0: LineSegment StartX=0 StartY=0 StartZ=0 EndX=44.4 EndY=0 EndZ=0
    g1: LineSegment StartX=44.4 StartY=0 StartZ=0 EndX=44.4 EndY=34.4 EndZ=0
    g2: LineSegment StartX=44.4 StartY=34.4 StartZ=0 EndX=0 EndY=34.4 EndZ=0
    g3: LineSegment StartX=0 StartY=34.4 StartZ=0 EndX=0 EndY=0 EndZ=0
  constraints (11):
    c: Coincident(g0,g1)
    c: Coincident(g1,g2)
    c: Coincident(g2,g3)
    c: Coincident(g3,g0)
    c: Horizontal(g0)
    c: Horizontal(g2)
    c: Vertical(g1)
    c: Vertical(g3)
    c: Coincident(g0,g-1)
    c: Distance(g2) = 44.4  'enclosure_length'
    c: Distance(g1) = 34.4  'case_width'
FEATURE [PartDesign::Pad] Pad002  label="Initial Pad001"
  Direction = (1,1,1)
  Length = 18.3
  Length2 = 100
  Profile = -> Sketch018
  Type = 0
  expr: Length = Spreadsheet.case_heigth
FEATURE [PartDesign::Fillet] Fillet002  label="Case Fillet001"
  Base = -> Pad002 [Edge9,Edge3,Edge10,Edge4]
  BaseFeature = -> Pad002
  Radius = 2
  SupportTransform = false
  expr: Radius = Spreadsheet.case_external_fillet
FEATURE [Sketcher::SketchObject] Sketch019  label="db9_male_hole001"
  FullyConstrained = true
  MapMode = 5
  Placement = pos=(44.4,0,0) rot=(0.57735,0.57735,0.57735;2.0944rad)
  Support = -> [Fillet002]
  expr: Constraints[28] = Spreadsheet.case_db9_hole_center_height
  expr: Constraints[19] = Spreadsheet.case_wall_thickness + Spreadsheet.clearance + Spreadsheet.db9_left_side_offset + Spreadsheet.db9_shield_width / 2
  expr: Constraints[18] = Spreadsheet.db9_connector_max_heigth + 2 * Spreadsheet.connector_clearance
  expr: Constraints[11] = Spreadsheet.db9_connector_max_width / 2 + Spreadsheet.connector_clearance
  sketch-geometry (12):
    g0: LineSegment StartX=9.36 StartY=14.95 StartZ=0 EndX=24.88 EndY=14.95 EndZ=0
    g1: LineSegment StartX=26.3572 StartY=13.1895 StartZ=0 EndX=25.1053 EndY=6.08953 EndZ=0
    g2: LineSegment StartX=23.6281 StartY=4.85 StartZ=0 EndX=10.6119 EndY=4.85 EndZ=0
    g3: LineSegment StartX=9.13471 StartY=6.08953 StartZ=0 EndX=7.88279 EndY=13.1895 EndZ=0
    g4: LineSegment StartX=17.12 StartY=14.95 StartZ=0 EndX=17.12 EndY=0 EndZ=0
    g5: ArcOfCircle CenterX=9.36 CenterY=13.45 CenterZ=0 NormalX=0 NormalY=0 NormalZ=1 AngleXU=0 Radius=1.5 StartAngle=1.5708 EndAngle=3.31613
    g6: ArcOfCircle CenterX=24.88 CenterY=13.45 CenterZ=0 NormalX=0 NormalY=0 NormalZ=1 AngleXU=0 Radius=1.5 StartAngle=6.10865 EndAngle=7.85398
    g7: ArcOfCircle CenterX=23.6281 CenterY=6.35 CenterZ=0 NormalX=0 NormalY=0 NormalZ=1 AngleXU=0 Radius=1.5 StartAngle=4.71239 EndAngle=6.10865
    g8: ArcOfCircle CenterX=10.6119 CenterY=6.35 CenterZ=0 NormalX=0 NormalY=0 NormalZ=1 AngleXU=0 Radius=1.5 StartAngle=3.31613 EndAngle=4.71239
    g9: LineSegment StartX=7.86 StartY=14.95 StartZ=0 EndX=7.86 EndY=4.85 EndZ=0
    g10: LineSegment StartX=26.38 StartY=14.95 StartZ=0 EndX=26.38 EndY=4.85 EndZ=0
    g11: GeomPoint X=7.86 Y=9.9 Z=0
  constraints (29):
    c: Horizontal(g0)
    c: PointOnObject(g4,g-1)
    c: Tangent(g0,g5) = 1.5708
    c: Tangent(g3,g5) = 1.5708
    c: Tangent(g0,g6) = 1.5708
    c: Tangent(g1,g6) = 1.5708
    c: Tangent(g1,g7) = 1.5708
    c: Tangent(g2,g7) = 1.5708
    c: Tangent(g2,g8) = 1.5708
    c: Tangent(g3,g8) = 1.5708
    c: Vertical(g9)
    c: Distance(g9,g4) = 9.26
    c: Vertical(g10)
    c: Tangent(g6,g10)
    c: Symmetric(g0,g0,g4)
    c: Symmetric(g2,g2,g4)
    c: Angle(g4,g3) = 0.174533
    c: Symmetric(g3,g1,g4)
    c: Distance(g2,g0) = 10.1
    c: Distance(g4,g-2) = 17.12
    c: Radius(g5) = 1.5
    c: Radius(g8) = 1.5
    c: Horizontal(g4,g9)
    c: Horizontal(g2,g10)
    c: Horizontal(g9,g2)
    c: PointOnObject(g9,g0)
    c: Symmetric(g10,g9,g4)
    c: Symmetric(g9,g9,g11)
    c: Distance(g11,g-1) = 9.9
FEATURE [PartDesign::Pocket] Pocket006  label="DB9 Connector holes001"
  BaseFeature = -> Fillet002
  Length = 44.4
  Length2 = 100
  Profile = -> Sketch019
  Type = 0
  expr: Length = Spreadsheet.case_length
FEATURE [Sketcher::SketchObject] Sketch020  label="case_inner void001"
  AttachmentOffset = pos=(0,0,1.2) rot=(0,0,1;0rad)
  ExternalGeometry = -> [Pocket006]
  FullyConstrained = true
  MapMode = 5
  Placement = pos=(1.2,-3e-16,3e-16) rot=(0.57735,0.57735,0.57735;2.0944rad)
  Support = -> [YZ_Plane010]
  expr: Constraints[18] = Spreadsheet.case_wall_thickness
  expr: Constraints[17] = Spreadsheet.case_wall_thickness
  expr: Constraints[16] = Spreadsheet.case_wall_thickness
  expr: Constraints[15] = Spreadsheet.case_wall_thickness
  expr: .AttachmentOffset.Base.z = Spreadsheet.case_wall_thickness
  sketch-geometry (8):
    g0: LineSegment StartX=32.4 StartY=17.1 StartZ=0 EndX=2 EndY=17.1 EndZ=0
    g1: LineSegment StartX=1.2 StartY=16.3 StartZ=0 EndX=1.2 EndY=2 EndZ=0
    g2: LineSegment StartX=2 StartY=1.2 StartZ=0 EndX=32.4 EndY=1.2 EndZ=0
    g3: LineSegment StartX=33.2 StartY=2 StartZ=0 EndX=33.2 EndY=16.3 EndZ=0
    g4: ArcOfCircle CenterX=32.4 CenterY=16.3 CenterZ=0 NormalX=0 NormalY=0 NormalZ=1 AngleXU=0 Radius=0.8 StartAngle=3.4e-15 EndAngle=1.5708
    g5: ArcOfCircle CenterX=32.4 CenterY=2 CenterZ=0 NormalX=0 NormalY=0 NormalZ=1 AngleXU=0 Radius=0.8 StartAngle=4.71239 EndAngle=6.28319
    g6: ArcOfCircle CenterX=2 CenterY=2 CenterZ=0 NormalX=0 NormalY=0 NormalZ=1 AngleXU=0 Radius=0.8 StartAngle=3.14159 EndAngle=4.71239
    g7: ArcOfCircle CenterX=2 CenterY=16.3 CenterZ=0 NormalX=0 NormalY=0 NormalZ=1 AngleXU=0 Radius=0.8 StartAngle=1.5708 EndAngle=3.14159
  constraints (20):
    c: Tangent(g0,g4) = -1.5708
    c: Tangent(g3,g4) = -1.5708
    c: Tangent(g3,g5) = -1.5708
    c: Tangent(g2,g5) = -1.5708
    c: Tangent(g2,g6) = -1.5708
    c: Tangent(g1,g6) = -1.5708
    c: Tangent(g0,g7) = -1.5708
    c: Tangent(g1,g7) = -1.5708
    c: Horizontal(g0)
    c: Horizontal(g2)
    c: Vertical(g1)
    c: Vertical(g3)
    c: Equal(g7,g6)
    c: Equal(g6,g5)
    c: Equal(g5,g4)
    c: Distance(g0,g-3) = 1.2
    c: Distance(g3,g-5) = 1.2
    c: Distance(g1,g-9) = 1.2
    c: Distance(g2,g-7) = 1.2
    c: Vertical(g0,g-10)
FEATURE [PartDesign::Pocket] Pocket007  label="Case emptying001"
  BaseFeature = -> Pocket006
  Length = 42
  Length2 = 100
  Profile = -> Sketch020
  Reversed = true
  Type = 0
  expr: Length = Spreadsheet.case_length - 2 * Spreadsheet.case_wall_thickness
FEATURE [Sketcher::SketchObject] Sketch021  label="pcb_front_support_sketch001"
  ExternalGeometry = -> [Pocket007]
  FullyConstrained = true
  MapMode = 5
  Placement = pos=(-3e-16,3e-16,1.2) rot=(0,0,1;0rad)
  Support = -> [Pocket007]
  expr: Constraints[4] = Spreadsheet.case_wall_thickness + Spreadsheet.db9_bottom_hole_front_shield
  expr: Constraints[0] = Spreadsheet.case_wall_thickness + Spreadsheet.db9_bottom_hole_front_shield
  expr: Constraints[9] = Spreadsheet.m3_pass_through_hole_diam
  expr: Constraints[2] = Spreadsheet.db9_distance_screws / 2
  expr: Constraints[10] = Spreadsheet.m3_pole_radius
  sketch-geometry (13):
    g0: ArcOfCircle CenterX=10.7 CenterY=4.625 CenterZ=0 NormalX=0 NormalY=0 NormalZ=1 AngleXU=0 Radius=2.4 StartAngle=5.60805 EndAngle=10.0999
    g1: LineSegment StartX=1.4e-15 StartY=17.12 StartZ=0 EndX=10.7 EndY=17.12 EndZ=0
    g2: ArcOfCircle CenterX=13.4982 CenterY=2.38462 CenterZ=0 NormalX=0 NormalY=0 NormalZ=1 AngleXU=0 Radius=1.18462 StartAngle=2.46646 EndAngle=4.71239
    g3: ArcOfCircle CenterX=7.90176 CenterY=2.38462 CenterZ=0 NormalX=0 NormalY=0 NormalZ=1 AngleXU=0 Radius=1.18462 StartAngle=4.71239 EndAngle=6.95832
    g4: Circle CenterX=10.7 CenterY=4.625 CenterZ=0 NormalX=0 NormalY=0 NormalZ=1 AngleXU=0 Radius=1.5
    g5: GeomPoint X=10.7 Y=3.125 Z=0
    g6: LineSegment StartX=7.90176 StartY=1.2 StartZ=0 EndX=13.4982 EndY=1.2 EndZ=0
    g7: GeomPoint X=10.7 Y=1.2 Z=0
    g8: LineSegment StartX=7.8249 StartY=33.2 StartZ=0 EndX=13.5751 EndY=33.2 EndZ=0
    g9: ArcOfCircle CenterX=7.8249 CenterY=31.9169 CenterZ=0 NormalX=0 NormalY=0 NormalZ=1 AngleXU=0 Radius=1.28308 StartAngle=5.60805 EndAngle=7.85398
    g10: ArcOfCircle CenterX=10.7 CenterY=29.615 CenterZ=0 NormalX=0 NormalY=0 NormalZ=1 AngleXU=0 Radius=2.4 StartAngle=2.46646 EndAngle=6.95832
    g11: ArcOfCircle CenterX=13.5751 CenterY=31.9169 CenterZ=0 NormalX=0 NormalY=0 NormalZ=1 AngleXU=0 Radius=1.28308 StartAngle=1.5708 EndAngle=3.81672
    g12: GeomPoint X=10.7 Y=33.2 Z=0
  constraints (31):
    c: Distance(g0,g-2) = 10.7
    c: Horizontal(g1)
    c: Distance(g0,g1) = 12.495
    c: Symmetric(g-3,g-3,g1)
    c: Distance(g1) = 10.7
    c: Equal(g3,g2)
    c: Tangent(g0,g2) = 1.5708
    c: Tangent(g0,g3) = 1.5708
    c: Coincident(g4,g0)
    c: Diameter(g4) = 3
    c: Radius(g0) = 2.4
    c: PointOnObject(g5,g4)
    c: Vertical(g5,g0)
    c: Horizontal(g5,g0)
    c: Horizontal(g0,g0)
    c: Coincident(g6,g3)
    c: Horizontal(g6)
    c: Symmetric(g3,g2,g7)
    c: PointOnObject(g3,g-4)
    c: Tangent(g6,g2) = -1.5708
    c: Equal(g9,g11)
    c: Tangent(g10,g11) = 1.5708
    c: Tangent(g10,g9) = 1.5708
    c: Coincident(g8,g9)
    c: Horizontal(g8)
    c: Tangent(g8,g11) = 1.5708
    c: Symmetric(g10,g0,g1)
    c: Symmetric(g0,g9,g1)
    c: PointOnObject(g8,g-5)
    c: Symmetric(g8,g8,g12)
    c: Vertical(g12,g10)
FEATURE [PartDesign::Pad] Pad003  label="PCB front support001"
  BaseFeature = -> Pocket007
  Direction = (1,1,1)
  Length = 0.8
  Length2 = 100
  Profile = -> Sketch021
  Type = 2
  expr: Length = Spreadsheet.pcb_bottom_clearance
FEATURE [Sketcher::SketchObject] Sketch022  label="Bottom hole sketch001"
  ExternalGeometry = -> [Pad003]
  FullyConstrained = true
  MapMode = 5
  Placement = pos=(0,0,0) rot=(1,0,0;3.14159rad)
  Support = -> [Pad003]
  expr: Constraints[0] = Spreadsheet.m3_pass_through_hole_diam
  sketch-geometry (2):
    g0: Circle CenterX=10.7 CenterY=-4.625 CenterZ=0 NormalX=0 NormalY=0 NormalZ=1 AngleXU=0 Radius=1.5
    g1: Circle CenterX=10.7 CenterY=-29.615 CenterZ=0 NormalX=0 NormalY=0 NormalZ=1 AngleXU=0 Radius=1.5
  constraints (4):
    c: Diameter(g0) = 3
    c: Coincident(g0,g-3)
    c: Coincident(g1,g-4)
    c: Equal(g1,g0)
FEATURE [PartDesign::LinearPattern] LinearPattern002  label="Supports LinearPattern001"
  Direction = -> X_Axis010
  Length = 23.16
  Occurrences = 2
  expr: Length = Spreadsheet.pcb_hole_dist_connectors
FEATURE [Sketcher::SketchObject] Sketch026  label="Split wire right001"
  AttachmentOffset = pos=(0,0,44.4) rot=(0,0,1;0rad)
  FullyConstrained = true
  MapMode = 5
  Placement = pos=(44.4,-9.9e-15,9.9e-15) rot=(0.57735,0.57735,0.57735;2.0944rad)
  Support = -> [YZ_Plane010]
  expr: .AttachmentOffset.Base.x = 0
  expr: .AttachmentOffset.Base.z = Spreadsheet.case_length
  expr: Constraints[2] = Spreadsheet.case_width
  expr: Constraints[10] = <<Spreadsheet>>.case_wall_thickness
  expr: Constraints[11] = Spreadsheet.case_top_bottom_thickness + Spreadsheet.pcb_thickness
  expr: Constraints[14] = Spreadsheet.case_external_fillet * 2
  sketch-geometry (5):
    g0: LineSegment StartX=33.2 StartY=3.1 StartZ=0 EndX=34.4 EndY=3.1 EndZ=0
    g1: LineSegment StartX=1.2 StartY=3.1 StartZ=0 EndX=0 EndY=3.1 EndZ=0
    g2: LineSegment StartX=29.2 StartY=7.1 StartZ=0 EndX=5.2 EndY=7.1 EndZ=0
    g3: ArcOfCircle CenterX=5.2 CenterY=3.1 CenterZ=0 NormalX=0 NormalY=0 NormalZ=1 AngleXU=0 Radius=4 StartAngle=1.5708 EndAngle=3.14159
    g4: ArcOfCircle CenterX=29.2 CenterY=3.1 CenterZ=0 NormalX=0 NormalY=0 NormalZ=1 AngleXU=0 Radius=4 StartAngle=0 EndAngle=1.5708
  constraints (16):
    c: Coincident(g1,g3)
    c: Coincident(g4,g0)
    c: Distance(g0,g-2) = 34.4
    c: Horizontal(g3,g4)
    c: Horizontal(g1,g3)
    c: Horizontal(g2)
    c: Tangent(g2,g3) = -1.5708
    c: Tangent(g4,g2) = -1.5708
    c: Horizontal(g0,g4)
    c: PointOnObject(g1,g-2)
    c: Distance(g1,g-2) = 1.2
    c: Distance(g1,g-1) = 3.1
    c: Horizontal(g0,g1)
    c: Equal(g0,g1)
    c: Radius(g3) = 4
    c: Horizontal(g1)
FEATURE [Sketcher::SketchObject] Sketch027  label="Split wire sides001"
  ExternalGeometry = -> [Sketch026]
  FullyConstrained = true
  MapMode = 5
  Placement = pos=(0,0,0) rot=(0.57735,0.57735,0.57735;2.0944rad)
  Support = -> [YZ_Plane010]
  sketch-geometry (2):
    g0: LineSegment StartX=0 StartY=3.1 StartZ=0 EndX=1.2 EndY=3.1 EndZ=0
    g1: LineSegment StartX=33.2 StartY=3.1 StartZ=0 EndX=34.4 EndY=3.1 EndZ=0
  constraints (4):
    c: Coincident(g0,g-4)
    c: Coincident(g0,g-4)
    c: Coincident(g1,g-3)
    c: Coincident(g1,g-3)
FEATURE [PartDesign::Hole] Hole003  label="Bottom hole001"
  BaseFeature = -> Pad003
  Depth = 2
  DepthType = 0
  Diameter = 2.9
  DrillForDepth = false
  DrillPoint = 0
  DrillPointAngle = 118
  HoleCutCountersinkAngle = 90
  HoleCutCustomValues = false
  HoleCutDepth = 1.2
  HoleCutDiameter = 5.5
  HoleCutType = 2
  ModelActualThread = false
  Profile = -> Sketch022
  Tapered = false
  TaperedAngle = 90
  ThreadAngle = 60
  ThreadClass = 0
  ThreadCutOffInner = 0.0487139
  ThreadCutOffOuter = 0.0974279
  ThreadDirection = 0
  ThreadFit = 0
  ThreadPitch = 0.45
  ThreadSize = 8
  ThreadType = 1
  Threaded = false
  expr: Depth = Spreadsheet.case_wall_thickness + Spreadsheet.pcb_bottom_clearance
  expr: HoleCutDepth = Spreadsheet.case_wall_thickness
FEATURE [Sketcher::SketchObject] Sketch023  label="Middle cut sketch001"
  ExternalGeometry = -> [Hole003,Sketch021]
  FullyConstrained = true
  MapMode = 5
  Placement = pos=(0,0,2) rot=(1,0,0;3.14159rad)
  Support = -> [Hole003]
  sketch-geometry (8):
    g0: ArcOfCircle CenterX=10.7 CenterY=-4.625 CenterZ=0 NormalX=0 NormalY=0 NormalZ=1 AngleXU=0 Radius=2.4 StartAngle=3.25303 EndAngle=6.17175
    g1: LineSegment StartX=8.31489 StartY=-4.8919 StartZ=0 EndX=7.90176 EndY=-1.2 EndZ=0
    g2: LineSegment StartX=13.0851 StartY=-4.8919 StartZ=0 EndX=13.4982 EndY=-1.2 EndZ=0
    g3: ArcOfCircle CenterX=10.7 CenterY=-29.615 CenterZ=0 NormalX=0 NormalY=0 NormalZ=1 AngleXU=0 Radius=2.4 StartAngle=0.126458 EndAngle=3.01514
    g4: LineSegment StartX=8.31916 StartY=-29.3123 StartZ=0 EndX=7.8249 EndY=-33.2 EndZ=0
    g5: LineSegment StartX=13.0808 StartY=-29.3123 StartZ=0 EndX=13.5751 EndY=-33.2 EndZ=0
    g6: LineSegment StartX=7.8249 StartY=-33.2 StartZ=0 EndX=13.5751 EndY=-33.2 EndZ=0
    g7: LineSegment StartX=7.90176 StartY=-1.2 StartZ=0 EndX=13.4982 EndY=-1.2 EndZ=0
  constraints (16):
    c: Tangent(g0,g2) = -1.5708
    c: Tangent(g1,g0) = 1.5708
    c: Coincident(g5,g6)
    c: Coincident(g4,g6)
    c: Coincident(g2,g7)
    c: Coincident(g1,g7)
    c: Coincident(g3,g-5)
    c: PointOnObject(g3,g-5)
    c: Coincident(g0,g-6)
    c: Coincident(g1,g-8)
    c: Coincident(g2,g-8)
    c: PointOnObject(g0,g-6)
    c: Coincident(g4,g-7)
    c: Tangent(g3,g4) = -1.5708
    c: Tangent(g5,g3) = 1.5708
    c: Coincident(g5,g-7)
FEATURE [PartDesign::Pocket] Pocket008  label="Middle cut for pcb and DB9 foot001"
  BaseFeature = -> Hole003
  Length = 4.3
  Length2 = 100
  Profile = -> Sketch023
  Type = 0
  expr: Length = Spreadsheet.db9_foot_heigth + Spreadsheet.pcb_thickness + Spreadsheet.clearance
FEATURE [Sketcher::SketchObject] Sketch024  label="M3 threaded sketch001"
  ExternalGeometry = -> [Pocket008]
  FullyConstrained = true
  MapMode = 5
  Placement = pos=(0,0,6.3) rot=(1,0,0;3.14159rad)
  Support = -> [Pocket008]
  sketch-geometry (3):
    g0: Circle CenterX=10.7 CenterY=-4.625 CenterZ=0 NormalX=0 NormalY=0 NormalZ=1 AngleXU=0 Radius=0.5
    g1: LineSegment StartX=0 StartY=-17.12 StartZ=0 EndX=10.7 EndY=-17.12 EndZ=0
    g2: Circle CenterX=10.7 CenterY=-29.615 CenterZ=0 NormalX=0 NormalY=0 NormalZ=1 AngleXU=0 Radius=0.5
  constraints (7):
    c: Diameter(g0) = 1
    c: Horizontal(g1)
    c: Symmetric(g-3,g-3,g1)
    c: Vertical(g1,g0)
    c: Equal(g0,g2)
    c: Symmetric(g0,g2,g1)
    c: Coincident(g2,g-4)
FEATURE [PartDesign::Hole] Hole002  label="M3 threaded hole001"
  BaseFeature = -> Pocket008
  Depth = 7
  DepthType = 0
  Diameter = 2.05
  DrillForDepth = false
  DrillPoint = 0
  DrillPointAngle = 118
  HoleCutCountersinkAngle = 90
  HoleCutCustomValues = false
  HoleCutDepth = 0
  HoleCutDiameter = 6.1
  HoleCutType = 0
  ModelActualThread = false
  Profile = -> Sketch024
  Tapered = false
  TaperedAngle = 90
  ThreadAngle = 60
  ThreadClass = 0
  ThreadCutOffInner = 0.0487139
  ThreadCutOffOuter = 0.0974279
  ThreadDirection = 0
  ThreadFit = 0
  ThreadPitch = 0.45
  ThreadSize = 8
  ThreadType = 1
  Threaded = true
  expr: Depth = Spreadsheet.m3_threaded_hole_depth
FEATURE [PartDesign::MultiTransform] MultiTransform001  label="Supports replication001"
  BaseFeature = -> Hole002
  Originals = -> [Pad003,Hole003,Pocket008,Hole002]
  Transformations = -> [LinearPattern002]
FEATURE [PartDesign::Plane] DatumPlane001  label="Top Plane001"
  AttachmentOffset = pos=(0,0,18.3) rot=(0,0,1;0rad)
  Length = 82.2411
  MapMode = 5
  Placement = pos=(0,0,18.3) rot=(0,0,1;0rad)
  ResizeMode = 0
  Support = -> [XY_Plane010]
  Width = 72.2411
  expr: .AttachmentOffset.Base.z = Spreadsheet.case_heigth
FEATURE [Sketcher::SketchObject] Sketch028  label="Arrows logo001"
  FullyConstrained = true
  MapMode = 5
  Placement = pos=(0,0,18.3) rot=(0,0,1;0rad)
  Support = -> [DatumPlane001]
  expr: Constraints[15] = Spreadsheet.case_width / 2
  expr: Constraints[16] = Spreadsheet.case_length / 2
  sketch-geometry (6):
    g0: LineSegment StartX=21.6641 StartY=19.2 StartZ=0 EndX=18.2 EndY=17.2 EndZ=0
    g1: LineSegment StartX=18.2 StartY=17.2 StartZ=0 EndX=21.6641 EndY=15.2 EndZ=0
    g2: LineSegment StartX=21.6641 StartY=15.2 StartZ=0 EndX=21.6641 EndY=19.2 EndZ=0
    g3: LineSegment StartX=25.6641 StartY=19.2 StartZ=0 EndX=22.2 EndY=17.2 EndZ=0
    g4: LineSegment StartX=22.2 StartY=17.2 StartZ=0 EndX=25.6641 EndY=15.2 EndZ=0
    g5: LineSegment StartX=25.6641 StartY=15.2 StartZ=0 EndX=25.6641 EndY=19.2 EndZ=0
  constraints (18):
    c: Coincident(g1,g0)
    c: Coincident(g2,g1)
    c: Coincident(g2,g0)
    c: Vertical(g2)
    c: Angle(g2,g1) = 1.0472
    c: Angle(g1,g0) = 1.0472
    c: Coincident(g4,g3)
    c: Coincident(g5,g4)
    c: Coincident(g5,g3)
    c: Vertical(g5)
    c: Angle(g5,g4) = 1.0472
    c: Angle(g4,g3) = 1.0472
    c: Horizontal(g1,g4)
    c: Horizontal(g3,g0)
    c: Distance(g0,g5) = 4
    c: Distance(g0,g-1) = 17.2
    c: Distance(g3,g-2) = 22.2
    c: Distance(g5) = 4
FEATURE [Sketcher::SketchObject] Sketch029  label="MSX Logo001"
  AttachmentOffset = pos=(10.7,17.2,0) rot=(0,0,1;1.5708rad)
  FullyConstrained = false
  MapMode = 5
  Placement = pos=(10.7,17.2,18.3) rot=(0,0,1;1.5708rad)
  Support = -> [DatumPlane001]
  expr: .AttachmentOffset.Base.y = Spreadsheet.label_msx_vpos
  expr: .AttachmentOffset.Base.x = Spreadsheet.label_msx_hpos
  sketch-geometry (39):
    g0: BSplineCurve PolesCount=2 KnotsCount=2 Degree=1 IsPeriodic=0
    g1: BSplineCurve PolesCount=2 KnotsCount=2 Degree=1 IsPeriodic=0
    g2: BSplineCurve PolesCount=2 KnotsCount=2 Degree=1 IsPeriodic=0
    g3: BSplineCurve PolesCount=2 KnotsCount=2 Degree=1 IsPeriodic=0
    g4: BSplineCurve PolesCount=2 KnotsCount=2 Degree=1 IsPeriodic=0
    g5: BSplineCurve PolesCount=2 KnotsCount=2 Degree=1 IsPeriodic=0
    g6: BSplineCurve PolesCount=2 KnotsCount=2 Degree=1 IsPeriodic=0
    g7: BSplineCurve PolesCount=2 KnotsCount=2 Degree=1 IsPeriodic=0
    g8: BSplineCurve PolesCount=2 KnotsCount=2 Degree=1 IsPeriodic=0
    g9: BSplineCurve PolesCount=2 KnotsCount=2 Degree=1 IsPeriodic=0
    g10: BSplineCurve PolesCount=4 KnotsCount=2 Degree=3 IsPeriodic=0
    g11: BSplineCurve PolesCount=2 KnotsCount=2 Degree=1 IsPeriodic=0
    g12: BSplineCurve PolesCount=4 KnotsCount=2 Degree=3 IsPeriodic=0
    g13: BSplineCurve PolesCount=4 KnotsCount=2 Degree=3 IsPeriodic=0
    g14: BSplineCurve PolesCount=2 KnotsCount=2 Degree=1 IsPeriodic=0
    g15: BSplineCurve PolesCount=2 KnotsCount=2 Degree=1 IsPeriodic=0
    g16: BSplineCurve PolesCount=2 KnotsCount=2 Degree=1 IsPeriodic=0
    g17: BSplineCurve PolesCount=2 KnotsCount=2 Degree=1 IsPeriodic=0
    g18: BSplineCurve PolesCount=2 KnotsCount=2 Degree=1 IsPeriodic=0
    g19: BSplineCurve PolesCount=2 KnotsCount=2 Degree=1 IsPeriodic=0
    g20: BSplineCurve PolesCount=2 KnotsCount=2 Degree=1 IsPeriodic=0
    g21: BSplineCurve PolesCount=2 KnotsCount=2 Degree=1 IsPeriodic=0
    g22: BSplineCurve PolesCount=2 KnotsCount=2 Degree=1 IsPeriodic=0
    g23: BSplineCurve PolesCount=2 KnotsCount=2 Degree=1 IsPeriodic=0
    g24: BSplineCurve PolesCount=2 KnotsCount=2 Degree=1 IsPeriodic=0
    g25: BSplineCurve PolesCount=2 KnotsCount=2 Degree=1 IsPeriodic=0
    g26: BSplineCurve PolesCount=2 KnotsCount=2 Degree=1 IsPeriodic=0
    g27: BSplineCurve PolesCount=4 KnotsCount=2 Degree=3 IsPeriodic=0
    g28: BSplineCurve PolesCount=2 KnotsCount=2 Degree=1 IsPeriodic=0
    g29: BSplineCurve PolesCount=4 KnotsCount=2 Degree=3 IsPeriodic=0
    g30: BSplineCurve PolesCount=4 KnotsCount=2 Degree=3 IsPeriodic=0
    g31: BSplineCurve PolesCount=2 KnotsCount=2 Degree=1 IsPeriodic=0
    g32: BSplineCurve PolesCount=2 KnotsCount=2 Degree=1 IsPeriodic=0
    g33: BSplineCurve PolesCount=2 KnotsCount=2 Degree=1 IsPeriodic=0
    g34: BSplineCurve PolesCount=2 KnotsCount=2 Degree=1 IsPeriodic=0
    g35: BSplineCurve PolesCount=2 KnotsCount=2 Degree=1 IsPeriodic=0
    g36: BSplineCurve PolesCount=2 KnotsCount=2 Degree=1 IsPeriodic=0
    g37: BSplineCurve PolesCount=2 KnotsCount=2 Degree=1 IsPeriodic=0
    g38: BSplineCurve PolesCount=2 KnotsCount=2 Degree=1 IsPeriodic=0
  constraints (39):
    c: Coincident(g0,g1)
    c: Coincident(g1,g2)
    c: Coincident(g2,g3)
    c: Coincident(g3,g0)
    c: Coincident(g4,g5)
    c: Coincident(g5,g6)
    c: Coincident(g6,g7)
    c: Coincident(g7,g8)
    c: Coincident(g8,g9)
    c: Coincident(g9,g10)
    c: Coincident(g10,g11)
    c: Coincident(g11,g12)
    c: Coincident(g12,g13)
    c: Coincident(g13,g14)
    c: Coincident(g14,g15)
    c: Coincident(g15,g16)
    c: Coincident(g16,g17)
    c: Coincident(g17,g18)
    c: Coincident(g18,g19)
    c: Coincident(g19,g20)
    c: Coincident(g20,g21)
    c: Coincident(g21,g22)
    c: Coincident(g22,g23)
    c: Coincident(g23,g24)
    c: Coincident(g24,g25)
    c: Coincident(g25,g26)
    c: Coincident(g26,g27)
    c: Coincident(g27,g28)
    c: Coincident(g28,g29)
    c: Coincident(g29,g30)
    c: Coincident(g30,g31)
    c: Coincident(g31,g32)
    c: Coincident(g32,g33)
    c: Coincident(g33,g34)
    c: Coincident(g34,g35)
    c: Coincident(g35,g36)
    c: Coincident(g36,g37)
    c: Coincident(g37,g38)
    c: Coincident(g38,g4)
FEATURE [PartDesign::Pocket] Pocket009  label="MSX Logo pocket001"
  BaseFeature = -> MultiTransform001
  Length = 0.6
  Length2 = 100
  Profile = -> Sketch029
  Type = 0
  expr: Length = Spreadsheet.case_wall_thickness / 2
FEATURE [PartDesign::Pocket] Pocket010  label="Arrows Logo pocket001"
  BaseFeature = -> Pocket009
  Length = 0.6
  Length2 = 100
  Profile = -> Sketch028
  Type = 0
  expr: Length = Spreadsheet.case_wall_thickness / 2
FEATURE [Sketcher::SketchObject] Sketch030  label="MD Logo001"
  AttachmentOffset = pos=(33.7,17.2,0) rot=(0,0,1;1.5708rad)
  FullyConstrained = false
  MapMode = 5
  Placement = pos=(33.7,17.2,18.3) rot=(0,0,1;1.5708rad)
  Support = -> [Pocket010,DatumPlane001]
  expr: .AttachmentOffset.Base.y = Spreadsheet.label_md_vpos
  expr: .AttachmentOffset.Base.x = Spreadsheet.label_md_hpos
  sketch-geometry (50):
    g0: BSplineCurve PolesCount=2 KnotsCount=2 Degree=1 IsPeriodic=0
    g1: BSplineCurve PolesCount=2 KnotsCount=2 Degree=1 IsPeriodic=0
    g2: BSplineCurve PolesCount=2 KnotsCount=2 Degree=1 IsPeriodic=0
    g3: BSplineCurve PolesCount=2 KnotsCount=2 Degree=1 IsPeriodic=0
    g4: BSplineCurve PolesCount=2 KnotsCount=2 Degree=1 IsPeriodic=0
    g5: BSplineCurve PolesCount=2 KnotsCount=2 Degree=1 IsPeriodic=0
    g6: BSplineCurve PolesCount=2 KnotsCount=2 Degree=1 IsPeriodic=0
    g7: BSplineCurve PolesCount=2 KnotsCount=2 Degree=1 IsPeriodic=0
    g8: BSplineCurve PolesCount=2 KnotsCount=2 Degree=1 IsPeriodic=0
    g9: BSplineCurve PolesCount=2 KnotsCount=2 Degree=1 IsPeriodic=0
    g10: BSplineCurve PolesCount=2 KnotsCount=2 Degree=1 IsPeriodic=0
    g11: BSplineCurve PolesCount=2 KnotsCount=2 Degree=1 IsPeriodic=0
    g12: BSplineCurve PolesCount=4 KnotsCount=2 Degree=3 IsPeriodic=0
    g13: BSplineCurve PolesCount=2 KnotsCount=2 Degree=1 IsPeriodic=0
    g14: BSplineCurve PolesCount=4 KnotsCount=2 Degree=3 IsPeriodic=0
    g15: BSplineCurve PolesCount=2 KnotsCount=2 Degree=1 IsPeriodic=0
    g16: BSplineCurve PolesCount=4 KnotsCount=2 Degree=3 IsPeriodic=0
    g17: BSplineCurve PolesCount=4 KnotsCount=2 Degree=3 IsPeriodic=0
    g18: BSplineCurve PolesCount=2 KnotsCount=2 Degree=1 IsPeriodic=0
    g19: BSplineCurve PolesCount=2 KnotsCount=2 Degree=1 IsPeriodic=0
    g20: BSplineCurve PolesCount=4 KnotsCount=2 Degree=3 IsPeriodic=0
    g21: BSplineCurve PolesCount=2 KnotsCount=2 Degree=1 IsPeriodic=0
    g22: BSplineCurve PolesCount=4 KnotsCount=2 Degree=3 IsPeriodic=0
    g23: BSplineCurve PolesCount=2 KnotsCount=2 Degree=1 IsPeriodic=0
    g24: BSplineCurve PolesCount=4 KnotsCount=2 Degree=3 IsPeriodic=0
    g25: BSplineCurve PolesCount=2 KnotsCount=2 Degree=1 IsPeriodic=0
    g26: BSplineCurve PolesCount=4 KnotsCount=2 Degree=3 IsPeriodic=0
    g27: BSplineCurve PolesCount=2 KnotsCount=2 Degree=1 IsPeriodic=0
    g28: BSplineCurve PolesCount=4 KnotsCount=2 Degree=3 IsPeriodic=0
    g29: BSplineCurve PolesCount=2 KnotsCount=2 Degree=1 IsPeriodic=0
    g30: BSplineCurve PolesCount=4 KnotsCount=2 Degree=3 IsPeriodic=0
    g31: BSplineCurve PolesCount=2 KnotsCount=2 Degree=1 IsPeriodic=0
    g32: BSplineCurve PolesCount=2 KnotsCount=2 Degree=1 IsPeriodic=0
    g33: BSplineCurve PolesCount=4 KnotsCount=2 Degree=3 IsPeriodic=0
    g34: BSplineCurve PolesCount=2 KnotsCount=2 Degree=1 IsPeriodic=0
    g35: BSplineCurve PolesCount=4 KnotsCount=2 Degree=3 IsPeriodic=0
    g36: BSplineCurve PolesCount=2 KnotsCount=2 Degree=1 IsPeriodic=0
    g37: BSplineCurve PolesCount=2 KnotsCount=2 Degree=1 IsPeriodic=0
    g38: BSplineCurve PolesCount=4 KnotsCount=2 Degree=3 IsPeriodic=0
    g39: BSplineCurve PolesCount=2 KnotsCount=2 Degree=1 IsPeriodic=0
    g40: BSplineCurve PolesCount=4 KnotsCount=2 Degree=3 IsPeriodic=0
    g41: BSplineCurve PolesCount=2 KnotsCount=2 Degree=1 IsPeriodic=0
    g42: BSplineCurve PolesCount=4 KnotsCount=2 Degree=3 IsPeriodic=0
    g43: BSplineCurve PolesCount=4 KnotsCount=2 Degree=3 IsPeriodic=0
    g44: BSplineCurve PolesCount=2 KnotsCount=2 Degree=1 IsPeriodic=0
    g45: BSplineCurve PolesCount=4 KnotsCount=2 Degree=3 IsPeriodic=0
    g46: BSplineCurve PolesCount=2 KnotsCount=2 Degree=1 IsPeriodic=0
    g47: BSplineCurve PolesCount=4 KnotsCount=2 Degree=3 IsPeriodic=0
    g48: BSplineCurve PolesCount=4 KnotsCount=2 Degree=3 IsPeriodic=0
    g49: BSplineCurve PolesCount=2 KnotsCount=2 Degree=1 IsPeriodic=0
  constraints (50):
    c: Coincident(g0,g1)
    c: Coincident(g1,g2)
    c: Coincident(g2,g3)
    c: Coincident(g3,g4)
    c: Coincident(g4,g5)
    c: Coincident(g5,g6)
    c: Coincident(g6,g0)
    c: Coincident(g7,g8)
    c: Coincident(g8,g9)
    c: Coincident(g9,g10)
    c: Coincident(g10,g7)
    c: Coincident(g11,g12)
    c: Coincident(g12,g13)
    c: Coincident(g13,g14)
    c: Coincident(g14,g15)
    c: Coincident(g15,g16)
    c: Coincident(g16,g17)
    c: Coincident(g17,g18)
    c: Coincident(g18,g11)
    c: Coincident(g19,g20)
    c: Coincident(g20,g21)
    c: Coincident(g21,g22)
    c: Coincident(g22,g19)
    c: Coincident(g23,g24)
    c: Coincident(g24,g25)
    c: Coincident(g25,g26)
    c: Coincident(g26,g23)
    c: Coincident(g27,g28)
    c: Coincident(g28,g29)
    c: Coincident(g29,g30)
    c: Coincident(g30,g31)
    c: Coincident(g31,g27)
    c: Coincident(g32,g33)
    c: Coincident(g33,g34)
    c: Coincident(g34,g35)
    c: Coincident(g35,g36)
    c: Coincident(g36,g32)
    c: Coincident(g37,g38)
    c: Coincident(g38,g39)
    c: Coincident(g39,g40)
    c: Coincident(g40,g41)
    c: Coincident(g41,g37)
    c: Coincident(g42,g43)
    c: Coincident(g43,g44)
    c: Coincident(g44,g45)
    c: Coincident(g45,g46)
    c: Coincident(g46,g47)
    c: Coincident(g47,g48)
    c: Coincident(g48,g49)
    c: Coincident(g49,g42)
FEATURE [PartDesign::Pocket] Pocket011  label="MD Logo pocket001"
  BaseFeature = -> Pocket010
  Length = 0.6
  Length2 = 100
  Profile = -> Sketch030
  Type = 0
  expr: Length = Spreadsheet.case_wall_thickness / 2
FEATURE [PartDesign::LinearPattern] LinearPattern003
  BaseFeature = -> Pocket011
  Direction = -> Sketch029 [N_Axis]
  Length = 17.1
  Occurrences = 2
  Originals = -> [Pocket009,Pocket010,Pocket011]
  Reversed = true
  expr: Length = Spreadsheet.case_heigth - Spreadsheet.case_wall_thickness
FEATURE [Sketcher::SketchObject] Sketch032  label="Wire hole"
  ExternalGeometry = -> [Sketch019]
  FullyConstrained = true
  MapMode = 5
  Placement = pos=(0,0,0) rot=(0.57735,0.57735,0.57735;2.0944rad)
  Support = -> [YZ_Plane010]
  expr: Constraints[16] = Spreadsheet.cable_stress_relief_diam / 2
  expr: Constraints[17] = Spreadsheet.cable_stress_relief_diam / 2
  sketch-geometry (15):
    g0: LineSegment StartX=14.47 StartY=9.63953 StartZ=0 EndX=14.47 EndY=6.98953 EndZ=0
    g1: LineSegment StartX=14.47 StartY=6.98953 StartZ=0 EndX=19.77 EndY=6.98953 EndZ=0
    g2: LineSegment StartX=19.77 StartY=6.98953 StartZ=0 EndX=19.77 EndY=9.63953 EndZ=0
    g3: Circle CenterX=17.12 CenterY=9.63953 CenterZ=0 NormalX=0 NormalY=0 NormalZ=1 AngleXU=0 Radius=3.74767
    g4: LineSegment StartX=25.7313 StartY=9.63953 StartZ=0 EndX=17.12 EndY=9.63953 EndZ=0
    g5: LineSegment StartX=17.12 StartY=9.63953 StartZ=0 EndX=17.12 EndY=4.85 EndZ=0
    g6: ArcOfCircle CenterX=17.12 CenterY=9.63953 CenterZ=0 NormalX=0 NormalY=0 NormalZ=1 AngleXU=0 Radius=2.65 StartAngle=1e-15 EndAngle=3.14159
    g7: LineSegment StartX=23.6281 StartY=4.85 StartZ=0 EndX=10.6119 EndY=4.85 EndZ=0
    g8: LineSegment StartX=7.88279 StartY=13.1895 StartZ=0 EndX=9.13471 EndY=6.08953 EndZ=0
    g9: LineSegment StartX=26.3572 StartY=13.1895 StartZ=0 EndX=25.1053 EndY=6.08953 EndZ=0
    g10: ArcOfCircle CenterX=9.36 CenterY=13.45 CenterZ=0 NormalX=0 NormalY=0 NormalZ=1 AngleXU=0 Radius=1.5 StartAngle=1.5708 EndAngle=3.31613
    g11: ArcOfCircle CenterX=23.6281 CenterY=6.35 CenterZ=0 NormalX=0 NormalY=0 NormalZ=1 AngleXU=0 Radius=1.5 StartAngle=4.71239 EndAngle=6.10865
    g12: ArcOfCircle CenterX=10.6119 CenterY=6.35 CenterZ=0 NormalX=0 NormalY=0 NormalZ=1 AngleXU=0 Radius=1.5 StartAngle=3.31613 EndAngle=4.71239
    g13: ArcOfCircle CenterX=24.88 CenterY=13.45 CenterZ=0 NormalX=0 NormalY=0 NormalZ=1 AngleXU=0 Radius=1.5 StartAngle=6.10865 EndAngle=7.85398
    g14: LineSegment StartX=9.36 StartY=14.95 StartZ=0 EndX=24.88 EndY=14.95 EndZ=0
  constraints (35):
    c: Coincident(g0,g1)
    c: Coincident(g1,g2)
    c: PointOnObject(g0,g3)
    c: PointOnObject(g1,g3)
    c: Horizontal(g4)
    c: Symmetric(g-3,g-3,g5)
    c: Symmetric(g-4,g-4,g4)
    c: Vertical(g5)
    c: Coincident(g4,g5)
    c: Coincident(g3,g4)
    c: Coincident(g6,g3)
    c: PointOnObject(g6,g2)
    c: PointOnObject(g6,g4)
    c: PointOnObject(g2,g4)
    c: Coincident(g0,g6)
    c: Parallel(g0,g5)
    c: Radius(g6) = 2.65
    c: Distance(g2) = 2.65
    c: Equal(g0,g2)
    c: Coincident(g8,g-6)
    c: Coincident(g9,g-4)
    c: Coincident(g9,g-4)
    c: Coincident(g-6,g8)
    c: Coincident(g7,g-3)
    c: Coincident(g10,g-5)
    c: Tangent(g10,g8) = -1.5708
    c: Tangent(g11,g9) = 1.5708
    c: Tangent(g12,g7) = 1.5708
    c: Tangent(g12,g8) = -1.5708
    c: Tangent(g11,g7) = 1.5708
    c: Tangent(g6,g2,g6) = -1.5708
    c: Coincident(g13,g9)
    c: Tangent(g13,g-5) = 1.5708
    c: Coincident(g14,g10)
    c: Coincident(g14,g13)
FEATURE [Sketcher::SketchObject] Sketch025  label="Split wire left001"
  ExternalGeometry = -> [Sketch032,Sketch026]
  FullyConstrained = true
  MapMode = 5
  Placement = pos=(0,0,0) rot=(0.57735,0.57735,0.57735;2.0944rad)
  Support = -> [YZ_Plane010]
  expr: Constraints[14] = Spreadsheet.slice_sides_angle + 90
  sketch-geometry (7):
    g0: LineSegment StartX=23.9517 StartY=9.63953 StartZ=0 EndX=10.4483 EndY=9.63953 EndZ=0
    g1: ArcOfCircle CenterX=10.4483 CenterY=3.1 CenterZ=0 NormalX=0 NormalY=0 NormalZ=1 AngleXU=0 Radius=6.53953 StartAngle=1.5708 EndAngle=2.35619
    g2: ArcOfCircle CenterX=23.9517 CenterY=3.1 CenterZ=0 NormalX=0 NormalY=0 NormalZ=1 AngleXU=0 Radius=6.53953 StartAngle=0.785398 EndAngle=1.5708
    g3: LineSegment StartX=33.2 StartY=3.1 StartZ=0 EndX=28.5759 EndY=7.72414 EndZ=0
    g4: LineSegment StartX=33.2 StartY=3.1 StartZ=0 EndX=34.4 EndY=3.1 EndZ=0
    g5: LineSegment StartX=0 StartY=3.1 StartZ=0 EndX=1.2 EndY=3.1 EndZ=0
    g6: LineSegment StartX=1.2 StartY=3.1 StartZ=0 EndX=5.82414 EndY=7.72414 EndZ=0
  constraints (16):
    c: Horizontal(g0)
    c: Tangent(g0,g1) = -1.5708
    c: Tangent(g0,g2) = -1.5708
    c: Equal(g1,g2)
    c: PointOnObject(g-3,g0)
    c: Coincident(g-5,g3)
    c: Tangent(g3,g2) = -1.5708
    c: Coincident(g4,g3)
    c: Coincident(g4,g-5)
    c: Coincident(g5,g-4)
    c: Coincident(g5,g-4)
    c: Coincident(g6,g5)
    c: Tangent(g6,g1) = 1.5708
    c: Equal(g6,g3)
    c: Angle(g6,g5) = 2.35619
    c: PointOnObject(g1,g5)
FEATURE [PartDesign::Pad] Pad004  label="Wire hole pad"
  BaseFeature = -> LinearPattern003
  Direction = (1,1,1)
  Length = 1.2
  Length2 = 100
  Profile = -> Sketch032
  Type = 0
  expr: Length = Spreadsheet.case_wall_thickness
FEATURE [Part::Extrusion] Extrude003  label="Slice plane right"
  Base = -> Sketch026
  Dir = (1,-1e-16,1e-16)
  DirMode = 2
  FaceMakerClass = Part::FaceMakerBullseye
  LengthFwd = 0
  LengthRev = 1.2
  Solid = false
  Symmetric = false
  expr: LengthRev = Spreadsheet.case_wall_thickness
FEATURE [Part::Extrusion] Extrude004  label="Slice plane sides"
  Base = -> Sketch027
  Dir = (1,-1e-16,1e-16)
  DirMode = 2
  FaceMakerClass = Part::FaceMakerBullseye
  LengthFwd = 44.4
  LengthRev = 0
  Solid = false
  Symmetric = false
  expr: LengthFwd = Spreadsheet.case_length
FEATURE [Part::Extrusion] Extrude005  label="Slice plane left"
  Base = -> Sketch025
  Dir = (1,-1e-16,1e-16)
  DirMode = 2
  FaceMakerClass = Part::FaceMakerBullseye
  LengthFwd = 1.2
  LengthRev = 0
  Solid = false
  Symmetric = false
  expr: LengthFwd = Spreadsheet.case_wall_thickness
FEATURE [Sketcher::SketchObject] Sketch033
  ExternalGeometry = -> [Pad004]
  FullyConstrained = true
  MapMode = 5
  Placement = pos=(0,0,6.3) rot=(1,0,0;3.14159rad)
  Support = -> [Pad004]
  sketch-geometry (12):
    g0: Circle CenterX=10.7 CenterY=-4.625 CenterZ=0 NormalX=0 NormalY=0 NormalZ=1 AngleXU=0 Radius=1.025
    g1: ArcOfCircle CenterX=10.7 CenterY=-4.625 CenterZ=0 NormalX=0 NormalY=0 NormalZ=1 AngleXU=0 Radius=2.4 StartAngle=2.46646 EndAngle=6.95832
    g2: ArcOfCircle CenterX=7.90176 CenterY=-2.38462 CenterZ=0 NormalX=0 NormalY=0 NormalZ=1 AngleXU=0 Radius=1.18462 StartAngle=5.60805 EndAngle=7.85398
    g3: LineSegment StartX=7.90176 StartY=-1.2 StartZ=0 EndX=13.4982 EndY=-1.2 EndZ=0
    g4: ArcOfCircle CenterX=13.4982 CenterY=-2.38462 CenterZ=0 NormalX=0 NormalY=0 NormalZ=1 AngleXU=0 Radius=1.18462 StartAngle=1.5708 EndAngle=3.81672
    g5: GeomPoint X=10.7 Y=-3.6 Z=0
    g6: Circle CenterX=10.7 CenterY=-29.615 CenterZ=0 NormalX=0 NormalY=0 NormalZ=1 AngleXU=0 Radius=1.025
    g7: GeomPoint X=10.7 Y=-28.59 Z=0
    g8: ArcOfCircle CenterX=10.7 CenterY=-29.615 CenterZ=0 NormalX=0 NormalY=0 NormalZ=1 AngleXU=0 Radius=2.4 StartAngle=5.60805 EndAngle=10.0999
    g9: ArcOfCircle CenterX=13.5751 CenterY=-31.9169 CenterZ=0 NormalX=0 NormalY=0 NormalZ=1 AngleXU=0 Radius=1.28308 StartAngle=2.46646 EndAngle=4.71239
    g10: LineSegment StartX=13.5751 StartY=-33.2 StartZ=0 EndX=7.8249 EndY=-33.2 EndZ=0
    g11: ArcOfCircle CenterX=7.8249 CenterY=-31.9169 CenterZ=0 NormalX=0 NormalY=0 NormalZ=1 AngleXU=0 Radius=1.28308 StartAngle=4.71239 EndAngle=6.95832
  constraints (24):
    c: Coincident(g0,g-4)
    c: Coincident(g1,g0)
    c: PointOnObject(g1,g-3)
    c: Coincident(g3,g-5)
    c: Coincident(g3,g-5)
    c: Tangent(g2,g1) = 1.5708
    c: Tangent(g2,g3) = 1.5708
    c: Tangent(g4,g3) = 1.5708
    c: Tangent(g4,g1) = 1.5708
    c: PointOnObject(g5,g0)
    c: Vertical(g0,g5)
    c: PointOnObject(g5,g-4)
    c: Coincident(g6,g-7)
    c: PointOnObject(g7,g6)
    c: Vertical(g7,g6)
    c: PointOnObject(g7,g-6)
    c: Coincident(g8,g6)
    c: PointOnObject(g8,g-7)
    c: Coincident(g9,g-8)
    c: Tangent(g9,g8) = 1.5708
    c: Coincident(g10,g-8)
    c: Tangent(g10,g9) = 1.5708
    c: Tangent(g11,g8) = 1.5708
    c: Tangent(g11,g10) = 1.5708
FEATURE [PartDesign::Pad] Pad005
  BaseFeature = -> Pad004
  Direction = (1,1,1)
  Length = 2.5
  Length2 = 100
  Profile = -> Sketch033
  Type = 0
  expr: Length = Spreadsheet.db9_foot_heigth
FEATURE [PartDesign::Fillet] Fillet003  label="Fillet last operation001"
  Base = -> Pad005 [Face2,Face5,Face11]
  BaseFeature = -> Pad005
  Radius = 1
  SupportTransform = false
  expr: Radius = Spreadsheet.case_front_rear_fillet
FEATURE [PartDesign::Body] Body001  label="case wired"
  Group = -> [DatumPlane001,Sketch018,Pad002,Fillet002,Sketch019,Pocket006,Sketch020,Pocket007,Sketch021,Pad003,Sketch022,Hole003,Pocket008,Hole002,Sketch024,Sketch023,MultiTransform001,Pocket009,LinearPattern002,Sketch029,Pocket010,Pocket011,Sketch028,Sketch030,LinearPattern003,Sketch032,Pad004,Sketch033,Pad005,Fillet003,Sketch026,Sketch027,Sketch025]
  Origin = -> Origin010
  Tip = -> Fillet003
FEATURE [App::Part] Part001  label="MSX Mega Adapter Case Wired"
  Group = -> [Body001]
  Origin = -> Origin009
FEATURE [Part::FeaturePython] Slice001  # WARN: FeaturePython — macro-defined, semantics opaque (R4)
  Base = -> Body001
  Mode = 1
  Tolerance = 0
  Tools = -> [Extrude003,Extrude004,Extrude005]
FEATURE [Part::FeaturePython] Slice001_child0  label="Bottom wired"  # WARN: FeaturePython — macro-defined, semantics opaque (R4)
  Base = -> Slice001
  FilterType = 1
  Invert = false
  OverrideMaxVal = 0
  WindowFrom = 80
  WindowTo = 100
  items = 0
FEATURE [Part::FeaturePython] Slice001_child1  label="Top wired"  # WARN: FeaturePython — macro-defined, semantics opaque (R4)
  Base = -> Slice001
  FilterType = 1
  Invert = false
  OverrideMaxVal = 0
  WindowFrom = 80
  WindowTo = 100
  items = 1
FEATURE [App::DocumentObjectGroup] GrExplode_Slice001  label="MSX-Mega Adapter wired Slice"
  Group = -> [Slice001_child0,Slice001_child1]
FEATURE [Sketcher::SketchObject] Sketch034  label="Initial sketch002"
  FullyConstrained = true
  MapMode = 5
  Support = -> [XY_Plane011]
  expr: .Constraints.case_width = Spreadsheet001.case_width
  expr: .Constraints.enclosure_length = Spreadsheet001.case_length
  sketch-geometry (4):
    g0: LineSegment StartX=0 StartY=0 StartZ=0 EndX=44.4 EndY=0 EndZ=0
    g1: LineSegment StartX=44.4 StartY=0 StartZ=0 EndX=44.4 EndY=34.4 EndZ=0
    g2: LineSegment StartX=44.4 StartY=34.4 StartZ=0 EndX=0 EndY=34.4 EndZ=0
    g3: LineSegment StartX=0 StartY=34.4 StartZ=0 EndX=0 EndY=0 EndZ=0
  constraints (11):
    c: Coincident(g0,g1)
    c: Coincident(g1,g2)
    c: Coincident(g2,g3)
    c: Coincident(g3,g0)
    c: Horizontal(g0)
    c: Horizontal(g2)
    c: Vertical(g1)
    c: Vertical(g3)
    c: Coincident(g0,g-1)
    c: Distance(g2) = 44.4  'enclosure_length'
    c: Distance(g1) = 34.4  'case_width'
FEATURE [PartDesign::Pad] Pad006  label="Initial Pad002"
  Direction = (1,1,1)
  Length = 18.3
  Length2 = 100
  Profile = -> Sketch034
  Type = 0
  expr: Length = Spreadsheet001.case_heigth
FEATURE [PartDesign::Plane] DatumPlane002  label="Top Plane002"
  AttachmentOffset = pos=(0,0,18.3) rot=(0,0,1;0rad)
  Length = 82.2411
  MapMode = 5
  Placement = pos=(0,0,18.3) rot=(0,0,1;0rad)
  ResizeMode = 0
  Support = -> [XY_Plane011]
  Width = 72.2411
  expr: .AttachmentOffset.Base.z = Spreadsheet001.case_heigth
FEATURE [PartDesign::Fillet] Fillet005  label="Case Fillet002"
  Base = -> Pad006 [Edge9,Edge3,Edge10,Edge4]
  BaseFeature = -> Pad006
  Radius = 2
  SupportTransform = false
  expr: Radius = Spreadsheet001.case_external_fillet
FEATURE [Sketcher::SketchObject] Sketch035  label="db9_male_hole002"
  FullyConstrained = true
  MapMode = 5
  Placement = pos=(44.4,0,0) rot=(0.57735,0.57735,0.57735;2.0944rad)
  Support = -> [Fillet005]
  expr: Constraints[11] = Spreadsheet001.db9_connector_max_width / 2 + Spreadsheet001.connector_clearance
  expr: Constraints[18] = Spreadsheet001.db9_connector_max_heigth + 2 * Spreadsheet001.connector_clearance
  expr: Constraints[19] = Spreadsheet001.case_wall_thickness + Spreadsheet001.clearance + Spreadsheet001.db9_left_side_offset + Spreadsheet001.db9_shield_width / 2
  expr: Constraints[28] = Spreadsheet001.case_db9_hole_center_height
  sketch-geometry (12):
    g0: LineSegment StartX=9.36 StartY=14.95 StartZ=0 EndX=24.88 EndY=14.95 EndZ=0
    g1: LineSegment StartX=26.3572 StartY=13.1895 StartZ=0 EndX=25.1053 EndY=6.08953 EndZ=0
    g2: LineSegment StartX=23.6281 StartY=4.85 StartZ=0 EndX=10.6119 EndY=4.85 EndZ=0
    g3: LineSegment StartX=9.13471 StartY=6.08953 StartZ=0 EndX=7.88279 EndY=13.1895 EndZ=0
    g4: LineSegment StartX=17.12 StartY=14.95 StartZ=0 EndX=17.12 EndY=0 EndZ=0
    g5: ArcOfCircle CenterX=9.36 CenterY=13.45 CenterZ=0 NormalX=0 NormalY=0 NormalZ=1 AngleXU=0 Radius=1.5 StartAngle=1.5708 EndAngle=3.31613
    g6: ArcOfCircle CenterX=24.88 CenterY=13.45 CenterZ=0 NormalX=0 NormalY=0 NormalZ=1 AngleXU=0 Radius=1.5 StartAngle=6.10865 EndAngle=7.85398
    g7: ArcOfCircle CenterX=23.6281 CenterY=6.35 CenterZ=0 NormalX=0 NormalY=0 NormalZ=1 AngleXU=0 Radius=1.5 StartAngle=4.71239 EndAngle=6.10865
    g8: ArcOfCircle CenterX=10.6119 CenterY=6.35 CenterZ=0 NormalX=0 NormalY=0 NormalZ=1 AngleXU=0 Radius=1.5 StartAngle=3.31613 EndAngle=4.71239
    g9: LineSegment StartX=7.86 StartY=14.95 StartZ=0 EndX=7.86 EndY=4.85 EndZ=0
    g10: LineSegment StartX=26.38 StartY=14.95 StartZ=0 EndX=26.38 EndY=4.85 EndZ=0
    g11: GeomPoint X=7.86 Y=9.9 Z=0
  constraints (29):
    c: Horizontal(g0)
    c: PointOnObject(g4,g-1)
    c: Tangent(g0,g5) = 1.5708
    c: Tangent(g3,g5) = 1.5708
    c: Tangent(g0,g6) = 1.5708
    c: Tangent(g1,g6) = 1.5708
    c: Tangent(g1,g7) = 1.5708
    c: Tangent(g2,g7) = 1.5708
    c: Tangent(g2,g8) = 1.5708
    c: Tangent(g3,g8) = 1.5708
    c: Vertical(g9)
    c: Distance(g9,g4) = 9.26
    c: Vertical(g10)
    c: Tangent(g6,g10)
    c: Symmetric(g0,g0,g4)
    c: Symmetric(g2,g2,g4)
    c: Angle(g4,g3) = 0.174533
    c: Symmetric(g3,g1,g4)
    c: Distance(g2,g0) = 10.1
    c: Distance(g4,g-2) = 17.12
    c: Radius(g5) = 1.5
    c: Radius(g8) = 1.5
    c: Horizontal(g4,g9)
    c: Horizontal(g2,g10)
    c: Horizontal(g9,g2)
    c: PointOnObject(g9,g0)
    c: Symmetric(g10,g9,g4)
    c: Symmetric(g9,g9,g11)
    c: Distance(g11,g-1) = 9.9
FEATURE [PartDesign::Pocket] Pocket014  label="DB9 Connector holes002"
  BaseFeature = -> Fillet005
  Length = 44.4
  Length2 = 100
  Profile = -> Sketch035
  Type = 0
  expr: Length = Spreadsheet001.case_length
FEATURE [PartDesign::LinearPattern] LinearPattern005  label="Supports LinearPattern002"
  Direction = -> X_Axis011
  Length = 23.16
  Occurrences = 2
  expr: Length = Spreadsheet001.pcb_hole_dist_connectors
FEATURE [Spreadsheet::Sheet] Spreadsheet001
  cells = A1=Parameter description; B1=Parameter alias; C1(Parameter_alias)=Value; D1(Value)=; A2=PCB - Length; B2=pcb_length; C2(pcb_length)=42; A3=PCB - Width; B3=pcb_width; C3(pcb_width)=31.6; A4=PCB - Thickness; B4=pcb_thickness; C4(pcb_thickness)=1.6; A5=PCB - Bottom clearance; B5=pcb_bottom_clearance; C5(pcb_bottom_clearance)=0.8; A6=PCB - Hole distance between connectors; B6=pcb_hole_dist_connectors; C6(pcb_hole_dist_connectors)=23.16; A7=Clearance between PCB and case; B7=clearance; C7(clearance)=0.2; A8=Connector clearance; B8=connector_clearance; C8(connector_clearance)=0.8; A9=Electronics heigth; B9=electronics_heigth; C9(electronics_heigth)=12.4; A10=Case - Wall thickness; B10=case_wall_thickness; C10(case_wall_thickness)=1.2; A11=Case - Upper clearance; B11=case_upper_clearance; C11(case_upper_clearance)=0.5; A12=Case - Top/Bottom thickness; B12=case_top_bottom_thickness; C12(case_top_bottom_thickness)=1.5; A13=Case - Length; B13=case_length; C13(case_length)==pcb_length + 2 * case_wall_thickness; A14=Case - Width; B14=case_width; C14(case_width)==pcb_width + 2 * (clearance + case_wall_thickness); A15=Case - Heigth; B15=case_heigth; C15(case_heigth)==2 * case_top_bottom_thickness + pcb_bottom_clearance + pcb_thickness + electronics_heigth + case_upper_clearance; A16=Case - External fillet; B16=case_external_fillet; C16(case_external_fillet)=2; A17=Case - Front and rear faces fillet; B17=case_front_rear_fillet; C17(case_front_rear_fillet)=1; A18=Case - DB9 hole center height; B18=case_db9_hole_center_height; C18(case_db9_hole_center_height)==case_wall_thickness + pcb_bottom_clearance + pcb_thickness + db9_screw_hole_heigth; A19=DB9 - Shield width (A); B19=db9_shield_width; C19(db9_shield_width)=30.84; A20=DB9 - Distance between screws (B); B20=db9_distance_screws; C20(db9_distance_screws)=24.99; A21=DB9 - Connector max width (C); B21=db9_connector_max_width; C21(db9_connector_max_width)=16.92; A22=DB9 - Connector max heigth; B22=db9_connector_max_heigth; C22(db9_connector_max_heigth)=8.5; A23=DB9 - Screw hole heigth; B23=db9_screw_hole_heigth; C23(db9_screw_hole_heigth)=6.3; A24=DB9 - Distance from bottom hole to front shield; B24=db9_bottom_hole_front_shield; C24(db9_bottom_hole_front_shield)==8.08 + 1.42; A25=DB9 - Connector angle; B25=db9_connector_angle; C25(db9_connector_angle)=10; A26=DB9 - Bottom distance between shield and connector; B26=db9_bottom_shield_connector; C26(db9_bottom_shield_connector)=1; A27=DB9 - Left side offset; B27=db9_left_side_offset; C27(db9_left_side_offset)=0.3; A28=DB9 - Right side offset; B28=db9_right_side_offset; C28(db9_right_side_offset)=0.65; A29=DB9 - Foot heigth; B29=db9_foot_heigth; C29(db9_foot_heigth)=2.5; A30=M3 - Non-threaded hole diameter; B30=m3_non_threaded_hole_diam; C30(m3_non_threaded_hole_diam)=2.5; A31=M3 - Non-threaded hole depth; B31=m3_non_threaded_hole_depth; C31(m3_non_threaded_hole_depth)==case_top_bottom_thickness + pcb_bottom_clearance; A32=M3 - Threaded hole depth; B32=m3_threaded_hole_depth; C32(m3_threaded_hole_depth)=7; A33=M3 - Pass-through hole; B33=m3_pass_through_hole_diam; C33(m3_pass_through_hole_diam)=3; A34=M3 - Pole radius; B34=m3_pole_radius; C34(m3_pole_radius)=2.4; A35=M3 - Castellated diameter; B35=m3_castellated_diameter; C35(m3_castellated_diameter)=5; A36=M3 - Castellated angle; B36=m3_castellated_angle; C36(m3_castellated_angle)=45; A37=Label - MSX width; B37=label_msx_width; C37(label_msx_width)=15; A38=Label - MSX heigth; B38=label_msx_heigth; C38(label_msx_heigth)=6.211; A39=Label - MSX horizontal position; B39=label_msx_hpos; C39(label_msx_hpos)==case_wall_thickness + db9_bottom_hole_front_shield; A40=Label - MSX vertical position; B40=label_msx_vpos; C40(label_msx_vpos)==case_width / 2; A41=Label - MD horizontal position; B41=label_md_hpos; C41(label_md_hpos)==case_length - (case_wall_thickness + db9_bottom_hole_front_shield); A42=Label - MD vertical position; B42=label_md_vpos; C42(label_md_vpos)==case_width / 2; A43=Cable - Stress relief diameter; B43=cable_stress_relief_diam; C43(cable_stress_relief_diam)=6; A44=Slice - Sides angle; B44=slice_sides_angle; C44(slice_sides_angle)=45; A45=Label - AAMSX width; B45=label_aamsx_width; C45(label_aamsx_width)=38; A46=Label - AAMSX height; B46=label_aamsx_height; C46(label_aamsx_height)=9.821999999999999; A47=Label - AAMSX horizontal position; B47=label_aamsx_hpos; C47(label_aamsx_hpos)=3; A48=Label - AAMSX vertical position; B48=label_aamsx_vpos; C48(label_aamsx_vpos)=12.2
FEATURE [Sketcher::SketchObject] Sketch039  label="case_inner void002"
  AttachmentOffset = pos=(0,0,1.2) rot=(0,0,1;0rad)
  ExternalGeometry = -> [Pocket014]
  FullyConstrained = true
  MapMode = 5
  Placement = pos=(1.2,-3e-16,3e-16) rot=(0.57735,0.57735,0.57735;2.0944rad)
  Support = -> [YZ_Plane011]
  expr: .AttachmentOffset.Base.z = Spreadsheet001.case_wall_thickness
  expr: Constraints[15] = Spreadsheet001.case_wall_thickness
  expr: Constraints[16] = Spreadsheet001.case_wall_thickness
  expr: Constraints[17] = Spreadsheet001.case_wall_thickness
  expr: Constraints[18] = Spreadsheet001.case_wall_thickness
  sketch-geometry (8):
    g0: LineSegment StartX=32.4 StartY=17.1 StartZ=0 EndX=2 EndY=17.1 EndZ=0
    g1: LineSegment StartX=1.2 StartY=16.3 StartZ=0 EndX=1.2 EndY=2 EndZ=0
    g2: LineSegment StartX=2 StartY=1.2 StartZ=0 EndX=32.4 EndY=1.2 EndZ=0
    g3: LineSegment StartX=33.2 StartY=2 StartZ=0 EndX=33.2 EndY=16.3 EndZ=0
    g4: ArcOfCircle CenterX=32.4 CenterY=16.3 CenterZ=0 NormalX=0 NormalY=0 NormalZ=1 AngleXU=0 Radius=0.8 StartAngle=3.4e-15 EndAngle=1.5708
    g5: ArcOfCircle CenterX=32.4 CenterY=2 CenterZ=0 NormalX=0 NormalY=0 NormalZ=1 AngleXU=0 Radius=0.8 StartAngle=4.71239 EndAngle=6.28319
    g6: ArcOfCircle CenterX=2 CenterY=2 CenterZ=0 NormalX=0 NormalY=0 NormalZ=1 AngleXU=0 Radius=0.8 StartAngle=3.14159 EndAngle=4.71239
    g7: ArcOfCircle CenterX=2 CenterY=16.3 CenterZ=0 NormalX=0 NormalY=0 NormalZ=1 AngleXU=0 Radius=0.8 StartAngle=1.5708 EndAngle=3.14159
  constraints (20):
    c: Tangent(g0,g4) = -1.5708
    c: Tangent(g3,g4) = -1.5708
    c: Tangent(g3,g5) = -1.5708
    c: Tangent(g2,g5) = -1.5708
    c: Tangent(g2,g6) = -1.5708
    c: Tangent(g1,g6) = -1.5708
    c: Tangent(g0,g7) = -1.5708
    c: Tangent(g1,g7) = -1.5708
    c: Horizontal(g0)
    c: Horizontal(g2)
    c: Vertical(g1)
    c: Vertical(g3)
    c: Equal(g7,g6)
    c: Equal(g6,g5)
    c: Equal(g5,g4)
    c: Distance(g0,g-3) = 1.2
    c: Distance(g3,g-5) = 1.2
    c: Distance(g1,g-9) = 1.2
    c: Distance(g2,g-7) = 1.2
    c: Vertical(g0,g-10)
FEATURE [PartDesign::Pocket] Pocket015  label="Case emptying002"
  BaseFeature = -> Pocket014
  Length = 42
  Length2 = 100
  Profile = -> Sketch039
  Reversed = true
  Type = 0
  expr: Length = Spreadsheet001.case_length - 2 * Spreadsheet001.case_wall_thickness
FEATURE [Sketcher::SketchObject] Sketch038  label="pcb_front_support_sketch002"
  ExternalGeometry = -> [Pocket015]
  FullyConstrained = true
  MapMode = 5
  Placement = pos=(-3e-16,3e-16,1.2) rot=(0,0,1;0rad)
  Support = -> [Pocket015]
  expr: Constraints[10] = Spreadsheet001.m3_pole_radius
  expr: Constraints[2] = Spreadsheet001.db9_distance_screws / 2
  expr: Constraints[9] = Spreadsheet001.m3_pass_through_hole_diam
  expr: Constraints[0] = Spreadsheet001.case_wall_thickness + Spreadsheet001.db9_bottom_hole_front_shield
  expr: Constraints[4] = Spreadsheet001.case_wall_thickness + Spreadsheet001.db9_bottom_hole_front_shield
  sketch-geometry (13):
    g0: ArcOfCircle CenterX=10.7 CenterY=4.625 CenterZ=0 NormalX=0 NormalY=0 NormalZ=1 AngleXU=0 Radius=2.4 StartAngle=5.60805 EndAngle=10.0999
    g1: LineSegment StartX=1.4e-15 StartY=17.12 StartZ=0 EndX=10.7 EndY=17.12 EndZ=0
    g2: ArcOfCircle CenterX=13.4982 CenterY=2.38462 CenterZ=0 NormalX=0 NormalY=0 NormalZ=1 AngleXU=0 Radius=1.18462 StartAngle=2.46646 EndAngle=4.71239
    g3: ArcOfCircle CenterX=7.90176 CenterY=2.38462 CenterZ=0 NormalX=0 NormalY=0 NormalZ=1 AngleXU=0 Radius=1.18462 StartAngle=4.71239 EndAngle=6.95832
    g4: Circle CenterX=10.7 CenterY=4.625 CenterZ=0 NormalX=0 NormalY=0 NormalZ=1 AngleXU=0 Radius=1.5
    g5: GeomPoint X=10.7 Y=3.125 Z=0
    g6: LineSegment StartX=7.90176 StartY=1.2 StartZ=0 EndX=13.4982 EndY=1.2 EndZ=0
    g7: GeomPoint X=10.7 Y=1.2 Z=0
    g8: LineSegment StartX=7.8249 StartY=33.2 StartZ=0 EndX=13.5751 EndY=33.2 EndZ=0
    g9: ArcOfCircle CenterX=7.8249 CenterY=31.9169 CenterZ=0 NormalX=0 NormalY=0 NormalZ=1 AngleXU=0 Radius=1.28308 StartAngle=5.60805 EndAngle=7.85398
    g10: ArcOfCircle CenterX=10.7 CenterY=29.615 CenterZ=0 NormalX=0 NormalY=0 NormalZ=1 AngleXU=0 Radius=2.4 StartAngle=2.46646 EndAngle=6.95832
    g11: ArcOfCircle CenterX=13.5751 CenterY=31.9169 CenterZ=0 NormalX=0 NormalY=0 NormalZ=1 AngleXU=0 Radius=1.28308 StartAngle=1.5708 EndAngle=3.81672
    g12: GeomPoint X=10.7 Y=33.2 Z=0
  constraints (31):
    c: Distance(g0,g-2) = 10.7
    c: Horizontal(g1)
    c: Distance(g0,g1) = 12.495
    c: Symmetric(g-3,g-3,g1)
    c: Distance(g1) = 10.7
    c: Equal(g3,g2)
    c: Tangent(g0,g2) = 1.5708
    c: Tangent(g0,g3) = 1.5708
    c: Coincident(g4,g0)
    c: Diameter(g4) = 3
    c: Radius(g0) = 2.4
    c: PointOnObject(g5,g4)
    c: Vertical(g5,g0)
    c: Horizontal(g5,g0)
    c: Horizontal(g0,g0)
    c: Coincident(g6,g3)
    c: Horizontal(g6)
    c: Symmetric(g3,g2,g7)
    c: PointOnObject(g3,g-4)
    c: Tangent(g6,g2) = -1.5708
    c: Equal(g9,g11)
    c: Tangent(g10,g11) = 1.5708
    c: Tangent(g10,g9) = 1.5708
    c: Coincident(g8,g9)
    c: Horizontal(g8)
    c: Tangent(g8,g11) = 1.5708
    c: Symmetric(g10,g0,g1)
    c: Symmetric(g0,g9,g1)
    c: PointOnObject(g8,g-5)
    c: Symmetric(g8,g8,g12)
    c: Vertical(g12,g10)
FEATURE [PartDesign::Pad] Pad008  label="PCB front support002"
  BaseFeature = -> Pocket015
  Direction = (1,1,1)
  Length = 0.8
  Length2 = 100
  Profile = -> Sketch038
  Type = 2
  expr: Length = Spreadsheet001.pcb_bottom_clearance
FEATURE [Sketcher::SketchObject] Sketch037  label="Bottom hole sketch002"
  ExternalGeometry = -> [Pad008]
  FullyConstrained = true
  MapMode = 5
  Placement = pos=(0,0,0) rot=(1,0,0;3.14159rad)
  Support = -> [Pad008]
  expr: Constraints[0] = Spreadsheet001.m3_pass_through_hole_diam
  sketch-geometry (2):
    g0: Circle CenterX=10.7 CenterY=-4.625 CenterZ=0 NormalX=0 NormalY=0 NormalZ=1 AngleXU=0 Radius=1.5
    g1: Circle CenterX=10.7 CenterY=-29.615 CenterZ=0 NormalX=0 NormalY=0 NormalZ=1 AngleXU=0 Radius=1.5
  constraints (4):
    c: Diameter(g0) = 3
    c: Coincident(g0,g-3)
    c: Coincident(g1,g-4)
    c: Equal(g1,g0)
FEATURE [PartDesign::Hole] Hole004  label="Bottom hole002"
  BaseFeature = -> Pad008
  Depth = 2
  DepthType = 0
  Diameter = 2.9
  DrillForDepth = false
  DrillPoint = 0
  DrillPointAngle = 118
  HoleCutCountersinkAngle = 90
  HoleCutCustomValues = false
  HoleCutDepth = 1.2
  HoleCutDiameter = 5.5
  HoleCutType = 2
  ModelActualThread = false
  Profile = -> Sketch037
  Tapered = false
  TaperedAngle = 90
  ThreadAngle = 60
  ThreadClass = 0
  ThreadCutOffInner = 0.0487139
  ThreadCutOffOuter = 0.0974279
  ThreadDirection = 0
  ThreadFit = 0
  ThreadPitch = 0.45
  ThreadSize = 8
  ThreadType = 1
  Threaded = false
  expr: HoleCutDepth = Spreadsheet001.case_wall_thickness
  expr: Depth = Spreadsheet001.case_wall_thickness + Spreadsheet001.pcb_bottom_clearance
FEATURE [Sketcher::SketchObject] Sketch041  label="Arrows logo002"
  FullyConstrained = true
  MapMode = 5
  Placement = pos=(0,0,18.3) rot=(0,0,1;0rad)
  Support = -> [DatumPlane002]
  expr: Constraints[16] = Spreadsheet001.case_length / 2
  expr: Constraints[15] = Spreadsheet001.case_width / 2
  sketch-geometry (6):
    g0: LineSegment StartX=21.6641 StartY=19.2 StartZ=0 EndX=18.2 EndY=17.2 EndZ=0
    g1: LineSegment StartX=18.2 StartY=17.2 StartZ=0 EndX=21.6641 EndY=15.2 EndZ=0
    g2: LineSegment StartX=21.6641 StartY=15.2 StartZ=0 EndX=21.6641 EndY=19.2 EndZ=0
    g3: LineSegment StartX=25.6641 StartY=19.2 StartZ=0 EndX=22.2 EndY=17.2 EndZ=0
    g4: LineSegment StartX=22.2 StartY=17.2 StartZ=0 EndX=25.6641 EndY=15.2 EndZ=0
    g5: LineSegment StartX=25.6641 StartY=15.2 StartZ=0 EndX=25.6641 EndY=19.2 EndZ=0
  constraints (18):
    c: Coincident(g1,g0)
    c: Coincident(g2,g1)
    c: Coincident(g2,g0)
    c: Vertical(g2)
    c: Angle(g2,g1) = 1.0472
    c: Angle(g1,g0) = 1.0472
    c: Coincident(g4,g3)
    c: Coincident(g5,g4)
    c: Coincident(g5,g3)
    c: Vertical(g5)
    c: Angle(g5,g4) = 1.0472
    c: Angle(g4,g3) = 1.0472
    c: Horizontal(g1,g4)
    c: Horizontal(g3,g0)
    c: Distance(g0,g5) = 4
    c: Distance(g0,g-1) = 17.2
    c: Distance(g3,g-2) = 22.2
    c: Distance(g5) = 4
FEATURE [Sketcher::SketchObject] Sketch042  label="Wire hole001"
  ExternalGeometry = -> [Sketch035]
  FullyConstrained = true
  MapMode = 5
  Placement = pos=(0,0,0) rot=(0.57735,0.57735,0.57735;2.0944rad)
  Support = -> [YZ_Plane011]
  expr: Constraints[17] = Spreadsheet001.cable_stress_relief_diam / 2
  expr: Constraints[16] = Spreadsheet001.cable_stress_relief_diam / 2
  sketch-geometry (15):
    g0: LineSegment StartX=14.12 StartY=9.63953 StartZ=0 EndX=14.12 EndY=6.63953 EndZ=0
    g1: LineSegment StartX=14.12 StartY=6.63953 StartZ=0 EndX=20.12 EndY=6.63953 EndZ=0
    g2: LineSegment StartX=20.12 StartY=6.63953 StartZ=0 EndX=20.12 EndY=9.63953 EndZ=0
    g3: Circle CenterX=17.12 CenterY=9.63953 CenterZ=0 NormalX=0 NormalY=0 NormalZ=1 AngleXU=0 Radius=4.24264
    g4: LineSegment StartX=25.7313 StartY=9.63953 StartZ=0 EndX=17.12 EndY=9.63953 EndZ=0
    g5: LineSegment StartX=17.12 StartY=9.63953 StartZ=0 EndX=17.12 EndY=4.85 EndZ=0
    g6: ArcOfCircle CenterX=17.12 CenterY=9.63953 CenterZ=0 NormalX=0 NormalY=0 NormalZ=1 AngleXU=0 Radius=3 StartAngle=5.07e-14 EndAngle=3.14159
    g7: LineSegment StartX=23.6281 StartY=4.85 StartZ=0 EndX=10.6119 EndY=4.85 EndZ=0
    g8: LineSegment StartX=7.88279 StartY=13.1895 StartZ=0 EndX=9.13471 EndY=6.08953 EndZ=0
    g9: LineSegment StartX=26.3572 StartY=13.1895 StartZ=0 EndX=25.1053 EndY=6.08953 EndZ=0
    g10: ArcOfCircle CenterX=9.36 CenterY=13.45 CenterZ=0 NormalX=0 NormalY=0 NormalZ=1 AngleXU=0 Radius=1.5 StartAngle=1.5708 EndAngle=3.31613
    g11: ArcOfCircle CenterX=23.6281 CenterY=6.35 CenterZ=0 NormalX=0 NormalY=0 NormalZ=1 AngleXU=0 Radius=1.5 StartAngle=4.71239 EndAngle=6.10865
    g12: ArcOfCircle CenterX=10.6119 CenterY=6.35 CenterZ=0 NormalX=0 NormalY=0 NormalZ=1 AngleXU=0 Radius=1.5 StartAngle=3.31613 EndAngle=4.71239
    g13: ArcOfCircle CenterX=24.88 CenterY=13.45 CenterZ=0 NormalX=0 NormalY=0 NormalZ=1 AngleXU=0 Radius=1.5 StartAngle=6.10865 EndAngle=7.85398
    g14: LineSegment StartX=9.36 StartY=14.95 StartZ=0 EndX=24.88 EndY=14.95 EndZ=0
  constraints (35):
    c: Coincident(g0,g1)
    c: Coincident(g1,g2)
    c: PointOnObject(g0,g3)
    c: PointOnObject(g1,g3)
    c: Horizontal(g4)
    c: Symmetric(g-3,g-3,g5)
    c: Symmetric(g-4,g-4,g4)
    c: Vertical(g5)
    c: Coincident(g4,g5)
    c: Coincident(g3,g4)
    c: Coincident(g6,g3)
    c: PointOnObject(g6,g2)
    c: PointOnObject(g6,g4)
    c: PointOnObject(g2,g4)
    c: Coincident(g0,g6)
    c: Parallel(g0,g5)
    c: Radius(g6) = 3
    c: Distance(g2) = 3
    c: Equal(g0,g2)
    c: Coincident(g8,g-6)
    c: Coincident(g9,g-4)
    c: Coincident(g9,g-4)
    c: Coincident(g-6,g8)
    c: Coincident(g7,g-3)
    c: Coincident(g10,g-5)
    c: Tangent(g10,g8) = -1.5708
    c: Tangent(g11,g9) = 1.5708
    c: Tangent(g12,g7) = 1.5708
    c: Tangent(g12,g8) = -1.5708
    c: Tangent(g11,g7) = 1.5708
    c: Tangent(g6,g2,g6) = -1.5708
    c: Coincident(g13,g9)
    c: Tangent(g13,g-5) = 1.5708
    c: Coincident(g14,g10)
    c: Coincident(g14,g13)
FEATURE [Sketcher::SketchObject] Sketch044  label="MSX Logo002"
  AttachmentOffset = pos=(10.7,17.2,0) rot=(0,0,1;1.5708rad)
  FullyConstrained = false
  MapMode = 5
  Placement = pos=(10.7,17.2,18.3) rot=(0,0,1;1.5708rad)
  Support = -> [DatumPlane002]
  expr: .AttachmentOffset.Base.x = Spreadsheet001.label_msx_hpos
  expr: .AttachmentOffset.Base.y = Spreadsheet001.label_msx_vpos
  sketch-geometry (39):
    g0: BSplineCurve PolesCount=2 KnotsCount=2 Degree=1 IsPeriodic=0
    g1: BSplineCurve PolesCount=2 KnotsCount=2 Degree=1 IsPeriodic=0
    g2: BSplineCurve PolesCount=2 KnotsCount=2 Degree=1 IsPeriodic=0
    g3: BSplineCurve PolesCount=2 KnotsCount=2 Degree=1 IsPeriodic=0
    g4: BSplineCurve PolesCount=2 KnotsCount=2 Degree=1 IsPeriodic=0
    g5: BSplineCurve PolesCount=2 KnotsCount=2 Degree=1 IsPeriodic=0
    g6: BSplineCurve PolesCount=2 KnotsCount=2 Degree=1 IsPeriodic=0
    g7: BSplineCurve PolesCount=2 KnotsCount=2 Degree=1 IsPeriodic=0
    g8: BSplineCurve PolesCount=2 KnotsCount=2 Degree=1 IsPeriodic=0
    g9: BSplineCurve PolesCount=2 KnotsCount=2 Degree=1 IsPeriodic=0
    g10: BSplineCurve PolesCount=4 KnotsCount=2 Degree=3 IsPeriodic=0
    g11: BSplineCurve PolesCount=2 KnotsCount=2 Degree=1 IsPeriodic=0
    g12: BSplineCurve PolesCount=4 KnotsCount=2 Degree=3 IsPeriodic=0
    g13: BSplineCurve PolesCount=4 KnotsCount=2 Degree=3 IsPeriodic=0
    g14: BSplineCurve PolesCount=2 KnotsCount=2 Degree=1 IsPeriodic=0
    g15: BSplineCurve PolesCount=2 KnotsCount=2 Degree=1 IsPeriodic=0
    g16: BSplineCurve PolesCount=2 KnotsCount=2 Degree=1 IsPeriodic=0
    g17: BSplineCurve PolesCount=2 KnotsCount=2 Degree=1 IsPeriodic=0
    g18: BSplineCurve PolesCount=2 KnotsCount=2 Degree=1 IsPeriodic=0
    g19: BSplineCurve PolesCount=2 KnotsCount=2 Degree=1 IsPeriodic=0
    g20: BSplineCurve PolesCount=2 KnotsCount=2 Degree=1 IsPeriodic=0
    g21: BSplineCurve PolesCount=2 KnotsCount=2 Degree=1 IsPeriodic=0
    g22: BSplineCurve PolesCount=2 KnotsCount=2 Degree=1 IsPeriodic=0
    g23: BSplineCurve PolesCount=2 KnotsCount=2 Degree=1 IsPeriodic=0
    g24: BSplineCurve PolesCount=2 KnotsCount=2 Degree=1 IsPeriodic=0
    g25: BSplineCurve PolesCount=2 KnotsCount=2 Degree=1 IsPeriodic=0
    g26: BSplineCurve PolesCount=2 KnotsCount=2 Degree=1 IsPeriodic=0
    g27: BSplineCurve PolesCount=4 KnotsCount=2 Degree=3 IsPeriodic=0
    g28: BSplineCurve PolesCount=2 KnotsCount=2 Degree=1 IsPeriodic=0
    g29: BSplineCurve PolesCount=4 KnotsCount=2 Degree=3 IsPeriodic=0
    g30: BSplineCurve PolesCount=4 KnotsCount=2 Degree=3 IsPeriodic=0
    g31: BSplineCurve PolesCount=2 KnotsCount=2 Degree=1 IsPeriodic=0
    g32: BSplineCurve PolesCount=2 KnotsCount=2 Degree=1 IsPeriodic=0
    g33: BSplineCurve PolesCount=2 KnotsCount=2 Degree=1 IsPeriodic=0
    g34: BSplineCurve PolesCount=2 KnotsCount=2 Degree=1 IsPeriodic=0
    g35: BSplineCurve PolesCount=2 KnotsCount=2 Degree=1 IsPeriodic=0
    g36: BSplineCurve PolesCount=2 KnotsCount=2 Degree=1 IsPeriodic=0
    g37: BSplineCurve PolesCount=2 KnotsCount=2 Degree=1 IsPeriodic=0
    g38: BSplineCurve PolesCount=2 KnotsCount=2 Degree=1 IsPeriodic=0
  constraints (39):
    c: Coincident(g0,g1)
    c: Coincident(g1,g2)
    c: Coincident(g2,g3)
    c: Coincident(g3,g0)
    c: Coincident(g4,g5)
    c: Coincident(g5,g6)
    c: Coincident(g6,g7)
    c: Coincident(g7,g8)
    c: Coincident(g8,g9)
    c: Coincident(g9,g10)
    c: Coincident(g10,g11)
    c: Coincident(g11,g12)
    c: Coincident(g12,g13)
    c: Coincident(g13,g14)
    c: Coincident(g14,g15)
    c: Coincident(g15,g16)
    c: Coincident(g16,g17)
    c: Coincident(g17,g18)
    c: Coincident(g18,g19)
    c: Coincident(g19,g20)
    c: Coincident(g20,g21)
    c: Coincident(g21,g22)
    c: Coincident(g22,g23)
    c: Coincident(g23,g24)
    c: Coincident(g24,g25)
    c: Coincident(g25,g26)
    c: Coincident(g26,g27)
    c: Coincident(g27,g28)
    c: Coincident(g28,g29)
    c: Coincident(g29,g30)
    c: Coincident(g30,g31)
    c: Coincident(g31,g32)
    c: Coincident(g32,g33)
    c: Coincident(g33,g34)
    c: Coincident(g34,g35)
    c: Coincident(g35,g36)
    c: Coincident(g36,g37)
    c: Coincident(g37,g38)
    c: Coincident(g38,g4)
FEATURE [Sketcher::SketchObject] Sketch046  label="Middle cut sketch002"
  ExternalGeometry = -> [Hole004,Sketch038]
  FullyConstrained = true
  MapMode = 5
  Placement = pos=(0,0,2) rot=(1,0,0;3.14159rad)
  Support = -> [Hole004]
  sketch-geometry (8):
    g0: ArcOfCircle CenterX=10.7 CenterY=-4.625 CenterZ=0 NormalX=0 NormalY=0 NormalZ=1 AngleXU=0 Radius=2.4 StartAngle=3.25303 EndAngle=6.17175
    g1: LineSegment StartX=8.31489 StartY=-4.8919 StartZ=0 EndX=7.90176 EndY=-1.2 EndZ=0
    g2: LineSegment StartX=13.0851 StartY=-4.8919 StartZ=0 EndX=13.4982 EndY=-1.2 EndZ=0
    g3: ArcOfCircle CenterX=10.7 CenterY=-29.615 CenterZ=0 NormalX=0 NormalY=0 NormalZ=1 AngleXU=0 Radius=2.4 StartAngle=0.126458 EndAngle=3.01514
    g4: LineSegment StartX=8.31916 StartY=-29.3123 StartZ=0 EndX=7.8249 EndY=-33.2 EndZ=0
    g5: LineSegment StartX=13.0808 StartY=-29.3123 StartZ=0 EndX=13.5751 EndY=-33.2 EndZ=0
    g6: LineSegment StartX=7.8249 StartY=-33.2 StartZ=0 EndX=13.5751 EndY=-33.2 EndZ=0
    g7: LineSegment StartX=7.90176 StartY=-1.2 StartZ=0 EndX=13.4982 EndY=-1.2 EndZ=0
  constraints (16):
    c: Tangent(g0,g2) = -1.5708
    c: Tangent(g1,g0) = 1.5708
    c: Coincident(g5,g6)
    c: Coincident(g4,g6)
    c: Coincident(g2,g7)
    c: Coincident(g1,g7)
    c: Coincident(g3,g-5)
    c: PointOnObject(g3,g-5)
    c: Coincident(g0,g-6)
    c: Coincident(g1,g-8)
    c: Coincident(g2,g-8)
    c: PointOnObject(g0,g-6)
    c: Coincident(g4,g-7)
    c: Tangent(g3,g4) = -1.5708
    c: Tangent(g5,g3) = 1.5708
    c: Coincident(g5,g-7)
FEATURE [PartDesign::Pocket] Pocket016  label="Middle cut for pcb and DB9 foot002"
  BaseFeature = -> Hole004
  Length = 4.3
  Length2 = 100
  Profile = -> Sketch046
  Type = 0
  expr: Length = Spreadsheet001.db9_foot_heigth + Spreadsheet001.pcb_thickness + Spreadsheet001.clearance
FEATURE [Sketcher::SketchObject] Sketch043  label="M3 threaded sketch002"
  ExternalGeometry = -> [Pocket016]
  FullyConstrained = true
  MapMode = 5
  Placement = pos=(0,0,6.3) rot=(1,0,0;3.14159rad)
  Support = -> [Pocket016]
  sketch-geometry (3):
    g0: Circle CenterX=10.7 CenterY=-4.625 CenterZ=0 NormalX=0 NormalY=0 NormalZ=1 AngleXU=0 Radius=0.5
    g1: LineSegment StartX=0 StartY=-17.12 StartZ=0 EndX=10.7 EndY=-17.12 EndZ=0
    g2: Circle CenterX=10.7 CenterY=-29.615 CenterZ=0 NormalX=0 NormalY=0 NormalZ=1 AngleXU=0 Radius=0.5
  constraints (7):
    c: Diameter(g0) = 1
    c: Horizontal(g1)
    c: Symmetric(g-3,g-3,g1)
    c: Vertical(g1,g0)
    c: Equal(g0,g2)
    c: Symmetric(g0,g2,g1)
    c: Coincident(g2,g-4)
FEATURE [PartDesign::Hole] Hole005  label="M3 threaded hole002"
  BaseFeature = -> Pocket016
  Depth = 7
  DepthType = 0
  Diameter = 2.05
  DrillForDepth = false
  DrillPoint = 0
  DrillPointAngle = 118
  HoleCutCountersinkAngle = 90
  HoleCutCustomValues = false
  HoleCutDepth = 0
  HoleCutDiameter = 6.1
  HoleCutType = 0
  ModelActualThread = false
  Profile = -> Sketch043
  Tapered = false
  TaperedAngle = 90
  ThreadAngle = 60
  ThreadClass = 0
  ThreadCutOffInner = 0.0487139
  ThreadCutOffOuter = 0.0974279
  ThreadDirection = 0
  ThreadFit = 0
  ThreadPitch = 0.45
  ThreadSize = 8
  ThreadType = 1
  Threaded = true
  expr: Depth = Spreadsheet001.m3_threaded_hole_depth
FEATURE [PartDesign::MultiTransform] MultiTransform002  label="Supports replication002"
  BaseFeature = -> Hole005
  Originals = -> [Pad008,Hole004,Pocket016,Hole005]
  Transformations = -> [LinearPattern005]
FEATURE [PartDesign::Pocket] Pocket013  label="MSX Logo pocket002"
  BaseFeature = -> MultiTransform002
  Length = 0.6
  Length2 = 100
  Profile = -> Sketch044
  Type = 0
  expr: Length = Spreadsheet001.case_wall_thickness / 2
FEATURE [PartDesign::Pocket] Pocket017  label="Arrows Logo pocket002"
  BaseFeature = -> Pocket013
  Length = 0.6
  Length2 = 100
  Profile = -> Sketch041
  Type = 0
  expr: Length = Spreadsheet001.case_wall_thickness / 2
FEATURE [Sketcher::SketchObject] Sketch045  label="MD Logo002"
  AttachmentOffset = pos=(33.7,17.2,0) rot=(0,0,1;1.5708rad)
  FullyConstrained = false
  MapMode = 5
  Placement = pos=(33.7,17.2,18.3) rot=(0,0,1;1.5708rad)
  Support = -> [Pocket017,DatumPlane002]
  expr: .AttachmentOffset.Base.x = Spreadsheet001.label_md_hpos
  expr: .AttachmentOffset.Base.y = Spreadsheet001.label_md_vpos
  sketch-geometry (50):
    g0: BSplineCurve PolesCount=2 KnotsCount=2 Degree=1 IsPeriodic=0
    g1: BSplineCurve PolesCount=2 KnotsCount=2 Degree=1 IsPeriodic=0
    g2: BSplineCurve PolesCount=2 KnotsCount=2 Degree=1 IsPeriodic=0
    g3: BSplineCurve PolesCount=2 KnotsCount=2 Degree=1 IsPeriodic=0
    g4: BSplineCurve PolesCount=2 KnotsCount=2 Degree=1 IsPeriodic=0
    g5: BSplineCurve PolesCount=2 KnotsCount=2 Degree=1 IsPeriodic=0
    g6: BSplineCurve PolesCount=2 KnotsCount=2 Degree=1 IsPeriodic=0
    g7: BSplineCurve PolesCount=2 KnotsCount=2 Degree=1 IsPeriodic=0
    g8: BSplineCurve PolesCount=2 KnotsCount=2 Degree=1 IsPeriodic=0
    g9: BSplineCurve PolesCount=2 KnotsCount=2 Degree=1 IsPeriodic=0
    g10: BSplineCurve PolesCount=2 KnotsCount=2 Degree=1 IsPeriodic=0
    g11: BSplineCurve PolesCount=2 KnotsCount=2 Degree=1 IsPeriodic=0
    g12: BSplineCurve PolesCount=4 KnotsCount=2 Degree=3 IsPeriodic=0
    g13: BSplineCurve PolesCount=2 KnotsCount=2 Degree=1 IsPeriodic=0
    g14: BSplineCurve PolesCount=4 KnotsCount=2 Degree=3 IsPeriodic=0
    g15: BSplineCurve PolesCount=2 KnotsCount=2 Degree=1 IsPeriodic=0
    g16: BSplineCurve PolesCount=4 KnotsCount=2 Degree=3 IsPeriodic=0
    g17: BSplineCurve PolesCount=4 KnotsCount=2 Degree=3 IsPeriodic=0
    g18: BSplineCurve PolesCount=2 KnotsCount=2 Degree=1 IsPeriodic=0
    g19: BSplineCurve PolesCount=2 KnotsCount=2 Degree=1 IsPeriodic=0
    g20: BSplineCurve PolesCount=4 KnotsCount=2 Degree=3 IsPeriodic=0
    g21: BSplineCurve PolesCount=2 KnotsCount=2 Degree=1 IsPeriodic=0
    g22: BSplineCurve PolesCount=4 KnotsCount=2 Degree=3 IsPeriodic=0
    g23: BSplineCurve PolesCount=2 KnotsCount=2 Degree=1 IsPeriodic=0
    g24: BSplineCurve PolesCount=4 KnotsCount=2 Degree=3 IsPeriodic=0
    g25: BSplineCurve PolesCount=2 KnotsCount=2 Degree=1 IsPeriodic=0
    g26: BSplineCurve PolesCount=4 KnotsCount=2 Degree=3 IsPeriodic=0
    g27: BSplineCurve PolesCount=2 KnotsCount=2 Degree=1 IsPeriodic=0
    g28: BSplineCurve PolesCount=4 KnotsCount=2 Degree=3 IsPeriodic=0
    g29: BSplineCurve PolesCount=2 KnotsCount=2 Degree=1 IsPeriodic=0
    g30: BSplineCurve PolesCount=4 KnotsCount=2 Degree=3 IsPeriodic=0
    g31: BSplineCurve PolesCount=2 KnotsCount=2 Degree=1 IsPeriodic=0
    g32: BSplineCurve PolesCount=2 KnotsCount=2 Degree=1 IsPeriodic=0
    g33: BSplineCurve PolesCount=4 KnotsCount=2 Degree=3 IsPeriodic=0
    g34: BSplineCurve PolesCount=2 KnotsCount=2 Degree=1 IsPeriodic=0
    g35: BSplineCurve PolesCount=4 KnotsCount=2 Degree=3 IsPeriodic=0
    g36: BSplineCurve PolesCount=2 KnotsCount=2 Degree=1 IsPeriodic=0
    g37: BSplineCurve PolesCount=2 KnotsCount=2 Degree=1 IsPeriodic=0
    g38: BSplineCurve PolesCount=4 KnotsCount=2 Degree=3 IsPeriodic=0
    g39: BSplineCurve PolesCount=2 KnotsCount=2 Degree=1 IsPeriodic=0
    g40: BSplineCurve PolesCount=4 KnotsCount=2 Degree=3 IsPeriodic=0
    g41: BSplineCurve PolesCount=2 KnotsCount=2 Degree=1 IsPeriodic=0
    g42: BSplineCurve PolesCount=4 KnotsCount=2 Degree=3 IsPeriodic=0
    g43: BSplineCurve PolesCount=4 KnotsCount=2 Degree=3 IsPeriodic=0
    g44: BSplineCurve PolesCount=2 KnotsCount=2 Degree=1 IsPeriodic=0
    g45: BSplineCurve PolesCount=4 KnotsCount=2 Degree=3 IsPeriodic=0
    g46: BSplineCurve PolesCount=2 KnotsCount=2 Degree=1 IsPeriodic=0
    g47: BSplineCurve PolesCount=4 KnotsCount=2 Degree=3 IsPeriodic=0
    g48: BSplineCurve PolesCount=4 KnotsCount=2 Degree=3 IsPeriodic=0
    g49: BSplineCurve PolesCount=2 KnotsCount=2 Degree=1 IsPeriodic=0
  constraints (50):
    c: Coincident(g0,g1)
    c: Coincident(g1,g2)
    c: Coincident(g2,g3)
    c: Coincident(g3,g4)
    c: Coincident(g4,g5)
    c: Coincident(g5,g6)
    c: Coincident(g6,g0)
    c: Coincident(g7,g8)
    c: Coincident(g8,g9)
    c: Coincident(g9,g10)
    c: Coincident(g10,g7)
    c: Coincident(g11,g12)
    c: Coincident(g12,g13)
    c: Coincident(g13,g14)
    c: Coincident(g14,g15)
    c: Coincident(g15,g16)
    c: Coincident(g16,g17)
    c: Coincident(g17,g18)
    c: Coincident(g18,g11)
    c: Coincident(g19,g20)
    c: Coincident(g20,g21)
    c: Coincident(g21,g22)
    c: Coincident(g22,g19)
    c: Coincident(g23,g24)
    c: Coincident(g24,g25)
    c: Coincident(g25,g26)
    c: Coincident(g26,g23)
    c: Coincident(g27,g28)
    c: Coincident(g28,g29)
    c: Coincident(g29,g30)
    c: Coincident(g30,g31)
    c: Coincident(g31,g27)
    c: Coincident(g32,g33)
    c: Coincident(g33,g34)
    c: Coincident(g34,g35)
    c: Coincident(g35,g36)
    c: Coincident(g36,g32)
    c: Coincident(g37,g38)
    c: Coincident(g38,g39)
    c: Coincident(g39,g40)
    c: Coincident(g40,g41)
    c: Coincident(g41,g37)
    c: Coincident(g42,g43)
    c: Coincident(g43,g44)
    c: Coincident(g44,g45)
    c: Coincident(g45,g46)
    c: Coincident(g46,g47)
    c: Coincident(g47,g48)
    c: Coincident(g48,g49)
    c: Coincident(g49,g42)
FEATURE [PartDesign::Pocket] Pocket012  label="MD Logo pocket002"
  BaseFeature = -> Pocket017
  Length = 0.6
  Length2 = 100
  Profile = -> Sketch045
  Type = 0
  expr: Length = Spreadsheet001.case_wall_thickness / 2
FEATURE [PartDesign::Pad] Pad007  label="Wire hole pad001"
  BaseFeature = -> Pocket012
  Direction = (1,1,1)
  Length = 1.2
  Length2 = 100
  Profile = -> Sketch042
  Type = 0
  expr: Length = Spreadsheet001.case_wall_thickness
FEATURE [Sketcher::SketchObject] Sketch047  label="Split wire right002"
  AttachmentOffset = pos=(0,0,44.4) rot=(0,0,1;0rad)
  FullyConstrained = true
  MapMode = 5
  Placement = pos=(44.4,-9.9e-15,9.9e-15) rot=(0.57735,0.57735,0.57735;2.0944rad)
  Support = -> [YZ_Plane011]
  expr: Constraints[14] = Spreadsheet001.case_external_fillet * 2
  expr: Constraints[11] = Spreadsheet001.case_top_bottom_thickness + Spreadsheet001.pcb_thickness
  expr: Constraints[10] = <<Spreadsheet001>>.case_wall_thickness
  expr: Constraints[2] = Spreadsheet001.case_width
  expr: .AttachmentOffset.Base.z = Spreadsheet001.case_length
  expr: .AttachmentOffset.Base.x = 0
  sketch-geometry (5):
    g0: LineSegment StartX=33.2 StartY=3.1 StartZ=0 EndX=34.4 EndY=3.1 EndZ=0
    g1: LineSegment StartX=1.2 StartY=3.1 StartZ=0 EndX=0 EndY=3.1 EndZ=0
    g2: LineSegment StartX=29.2 StartY=7.1 StartZ=0 EndX=5.2 EndY=7.1 EndZ=0
    g3: ArcOfCircle CenterX=5.2 CenterY=3.1 CenterZ=0 NormalX=0 NormalY=0 NormalZ=1 AngleXU=0 Radius=4 StartAngle=1.5708 EndAngle=3.14159
    g4: ArcOfCircle CenterX=29.2 CenterY=3.1 CenterZ=0 NormalX=0 NormalY=0 NormalZ=1 AngleXU=0 Radius=4 StartAngle=0 EndAngle=1.5708
  constraints (16):
    c: Coincident(g1,g3)
    c: Coincident(g4,g0)
    c: Distance(g0,g-2) = 34.4
    c: Horizontal(g3,g4)
    c: Horizontal(g1,g3)
    c: Horizontal(g2)
    c: Tangent(g2,g3) = -1.5708
    c: Tangent(g4,g2) = -1.5708
    c: Horizontal(g0,g4)
    c: PointOnObject(g1,g-2)
    c: Distance(g1,g-2) = 1.2
    c: Distance(g1,g-1) = 3.1
    c: Horizontal(g0,g1)
    c: Equal(g0,g1)
    c: Radius(g3) = 4
    c: Horizontal(g1)
FEATURE [Sketcher::SketchObject] Sketch036  label="Split wire left002"
  ExternalGeometry = -> [Sketch042,Sketch047]
  FullyConstrained = true
  MapMode = 5
  Placement = pos=(0,0,0) rot=(0.57735,0.57735,0.57735;2.0944rad)
  Support = -> [YZ_Plane011]
  expr: Constraints[14] = Spreadsheet001.slice_sides_angle + 90
  sketch-geometry (7):
    g0: LineSegment StartX=23.9517 StartY=9.63953 StartZ=0 EndX=10.4483 EndY=9.63953 EndZ=0
    g1: ArcOfCircle CenterX=10.4483 CenterY=3.1 CenterZ=0 NormalX=0 NormalY=0 NormalZ=1 AngleXU=0 Radius=6.53953 StartAngle=1.5708 EndAngle=2.35619
    g2: ArcOfCircle CenterX=23.9517 CenterY=3.1 CenterZ=0 NormalX=0 NormalY=0 NormalZ=1 AngleXU=0 Radius=6.53953 StartAngle=0.785398 EndAngle=1.5708
    g3: LineSegment StartX=33.2 StartY=3.1 StartZ=0 EndX=28.5759 EndY=7.72414 EndZ=0
    g4: LineSegment StartX=33.2 StartY=3.1 StartZ=0 EndX=34.4 EndY=3.1 EndZ=0
    g5: LineSegment StartX=0 StartY=3.1 StartZ=0 EndX=1.2 EndY=3.1 EndZ=0
    g6: LineSegment StartX=1.2 StartY=3.1 StartZ=0 EndX=5.82414 EndY=7.72414 EndZ=0
  constraints (16):
    c: Horizontal(g0)
    c: Tangent(g0,g1) = -1.5708
    c: Tangent(g0,g2) = -1.5708
    c: Equal(g1,g2)
    c: PointOnObject(g-3,g0)
    c: Coincident(g-5,g3)
    c: Tangent(g3,g2) = -1.5708
    c: Coincident(g4,g3)
    c: Coincident(g4,g-5)
    c: Coincident(g5,g-4)
    c: Coincident(g5,g-4)
    c: Coincident(g6,g5)
    c: Tangent(g6,g1) = 1.5708
    c: Equal(g6,g3)
    c: Angle(g6,g5) = 2.35619
    c: PointOnObject(g1,g5)
FEATURE [Part::Extrusion] Extrude006  label="Slice plane right001"
  Base = -> Sketch047
  Dir = (1,-1e-16,1e-16)
  DirMode = 2
  FaceMakerClass = Part::FaceMakerBullseye
  LengthFwd = 0
  LengthRev = 1.2
  Solid = false
  Symmetric = false
  expr: LengthRev = Spreadsheet001.case_wall_thickness
FEATURE [Sketcher::SketchObject] Sketch040  label="Split wire sides002"
  ExternalGeometry = -> [Sketch047]
  FullyConstrained = true
  MapMode = 5
  Placement = pos=(0,0,0) rot=(0.57735,0.57735,0.57735;2.0944rad)
  Support = -> [YZ_Plane011]
  sketch-geometry (2):
    g0: LineSegment StartX=0 StartY=3.1 StartZ=0 EndX=1.2 EndY=3.1 EndZ=0
    g1: LineSegment StartX=33.2 StartY=3.1 StartZ=0 EndX=34.4 EndY=3.1 EndZ=0
  constraints (4):
    c: Coincident(g0,g-4)
    c: Coincident(g0,g-4)
    c: Coincident(g1,g-3)
    c: Coincident(g1,g-3)
FEATURE [Part::Extrusion] Extrude007  label="Slice plane sides001"
  Base = -> Sketch040
  Dir = (1,-1e-16,1e-16)
  DirMode = 2
  FaceMakerClass = Part::FaceMakerBullseye
  LengthFwd = 44.4
  LengthRev = 0
  Solid = false
  Symmetric = false
  expr: LengthFwd = Spreadsheet001.case_length
FEATURE [Part::Extrusion] Extrude008  label="Slice plane left001"
  Base = -> Sketch036
  Dir = (1,-1e-16,1e-16)
  DirMode = 2
  FaceMakerClass = Part::FaceMakerBullseye
  LengthFwd = 1.2
  LengthRev = 0
  Solid = false
  Symmetric = false
  expr: LengthFwd = Spreadsheet001.case_wall_thickness
FEATURE [Sketcher::SketchObject] Sketch048
  ExternalGeometry = -> [Pad007]
  FullyConstrained = true
  MapMode = 5
  Placement = pos=(0,0,6.3) rot=(1,0,0;3.14159rad)
  Support = -> [Pocket012]
  sketch-geometry (10):
    g0: Circle CenterX=10.7 CenterY=-4.625 CenterZ=0 NormalX=0 NormalY=0 NormalZ=1 AngleXU=0 Radius=1.025
    g1: ArcOfCircle CenterX=10.7 CenterY=-4.625 CenterZ=0 NormalX=0 NormalY=0 NormalZ=1 AngleXU=0 Radius=2.4 StartAngle=2.46646 EndAngle=6.95832
    g2: ArcOfCircle CenterX=7.90176 CenterY=-2.38462 CenterZ=0 NormalX=0 NormalY=0 NormalZ=1 AngleXU=0 Radius=1.18462 StartAngle=5.60805 EndAngle=7.85398
    g3: LineSegment StartX=7.90176 StartY=-1.2 StartZ=0 EndX=13.4982 EndY=-1.2 EndZ=0
    g4: ArcOfCircle CenterX=13.4982 CenterY=-2.38462 CenterZ=0 NormalX=0 NormalY=0 NormalZ=1 AngleXU=0 Radius=1.18462 StartAngle=1.5708 EndAngle=3.81672
    g5: Circle CenterX=10.7 CenterY=-29.615 CenterZ=0 NormalX=0 NormalY=0 NormalZ=1 AngleXU=0 Radius=1.025
    g6: ArcOfCircle CenterX=10.7 CenterY=-29.615 CenterZ=0 NormalX=0 NormalY=0 NormalZ=1 AngleXU=0 Radius=2.4 StartAngle=5.60805 EndAngle=10.0999
    g7: ArcOfCircle CenterX=13.5751 CenterY=-31.9169 CenterZ=0 NormalX=0 NormalY=0 NormalZ=1 AngleXU=0 Radius=1.28308 StartAngle=2.46646 EndAngle=4.71239
    g8: LineSegment StartX=13.5751 StartY=-33.2 StartZ=0 EndX=7.8249 EndY=-33.2 EndZ=0
    g9: ArcOfCircle CenterX=7.8249 CenterY=-31.9169 CenterZ=0 NormalX=0 NormalY=0 NormalZ=1 AngleXU=0 Radius=1.28308 StartAngle=4.71239 EndAngle=6.95832
  constraints (20):
    c: Coincident(g1,g0)
    c: Tangent(g2,g1) = 1.5708
    c: Tangent(g2,g3) = 1.5708
    c: Tangent(g4,g3) = 1.5708
    c: Tangent(g4,g1) = 1.5708
    c: Coincident(g6,g5)
    c: Tangent(g7,g6) = 1.5708
    c: Tangent(g8,g7) = 1.5708
    c: Tangent(g9,g6) = 1.5708
    c: Tangent(g9,g8) = 1.5708
    c: Coincident(g2,g-5)
    c: Coincident(g3,g-5)
    c: Coincident(g-3,g0)
    c: Equal(g0,g-3)
    c: Equal(g1,g-6)
    c: Equal(g5,g-7)
    c: Coincident(g5,g-7)
    c: Coincident(g8,g-8)
    c: Coincident(g7,g-8)
    c: Equal(g6,g-9)
FEATURE [PartDesign::Pad] Pad009
  BaseFeature = -> Pad007
  Direction = (1,1,1)
  Length = 2.5
  Length2 = 100
  Profile = -> Sketch048
  Type = 0
  expr: Length = Spreadsheet001.db9_foot_heigth
FEATURE [PartDesign::Fillet] Fillet004  label="Fillet last operation002"
  Base = -> Pad009 [Face2,Face5,Face11]
  BaseFeature = -> Pad009
  Radius = 1
  SupportTransform = false
  expr: Radius = Spreadsheet001.case_front_rear_fillet
FEATURE [Sketcher::SketchObject] Sketch049  label="AAMSX Logo Window"
  AttachmentOffset = pos=(3,12.2,0) rot=(0,0,1;3.14159rad)
  FullyConstrained = false
  MapMode = 5
  Placement = pos=(3,12.2,0) rot=(0,0,1;3.14159rad)
  Support = -> [XY_Plane011]
  expr: .AttachmentOffset.Base.y = Spreadsheet001.label_aamsx_vpos
  expr: .AttachmentOffset.Base.x = Spreadsheet001.label_aamsx_hpos
  sketch-geometry (4):
    g0: BSplineCurve PolesCount=2 KnotsCount=2 Degree=1 IsPeriodic=0
    g1: BSplineCurve PolesCount=2 KnotsCount=2 Degree=1 IsPeriodic=0
    g2: BSplineCurve PolesCount=2 KnotsCount=2 Degree=1 IsPeriodic=0
    g3: BSplineCurve PolesCount=2 KnotsCount=2 Degree=1 IsPeriodic=0
  constraints (4):
    c: Coincident(g0,g1)
    c: Coincident(g1,g2)
    c: Coincident(g2,g3)
    c: Coincident(g3,g0)
FEATURE [Sketcher::SketchObject] Sketch050  label="AAMSX Logo Text"
  AttachmentOffset = pos=(3,12.2,0) rot=(0,0,1;3.14159rad)
  FullyConstrained = false
  MapMode = 5
  Placement = pos=(3,12.2,0) rot=(0,0,1;3.14159rad)
  Support = -> [XY_Plane011]
  expr: .AttachmentOffset.Base.x = Spreadsheet001.label_aamsx_hpos
  expr: .AttachmentOffset.Base.y = Spreadsheet001.label_aamsx_vpos
  sketch-geometry (59):
    g0: BSplineCurve PolesCount=2 KnotsCount=2 Degree=1 IsPeriodic=0
    g1: BSplineCurve PolesCount=2 KnotsCount=2 Degree=1 IsPeriodic=0
    g2: BSplineCurve PolesCount=2 KnotsCount=2 Degree=1 IsPeriodic=0
    g3: BSplineCurve PolesCount=2 KnotsCount=2 Degree=1 IsPeriodic=0
    g4: BSplineCurve PolesCount=2 KnotsCount=2 Degree=1 IsPeriodic=0
    g5: BSplineCurve PolesCount=2 KnotsCount=2 Degree=1 IsPeriodic=0
    g6: BSplineCurve PolesCount=2 KnotsCount=2 Degree=1 IsPeriodic=0
    g7: BSplineCurve PolesCount=2 KnotsCount=2 Degree=1 IsPeriodic=0
    g8: BSplineCurve PolesCount=2 KnotsCount=2 Degree=1 IsPeriodic=0
    g9: BSplineCurve PolesCount=2 KnotsCount=2 Degree=1 IsPeriodic=0
    g10: BSplineCurve PolesCount=4 KnotsCount=2 Degree=3 IsPeriodic=0
    g11: BSplineCurve PolesCount=4 KnotsCount=2 Degree=3 IsPeriodic=0
    g12: BSplineCurve PolesCount=2 KnotsCount=2 Degree=1 IsPeriodic=0
    g13: BSplineCurve PolesCount=4 KnotsCount=2 Degree=3 IsPeriodic=0
    g14: BSplineCurve PolesCount=4 KnotsCount=2 Degree=3 IsPeriodic=0
    g15: BSplineCurve PolesCount=2 KnotsCount=2 Degree=1 IsPeriodic=0
    g16: BSplineCurve PolesCount=2 KnotsCount=2 Degree=1 IsPeriodic=0
    g17: BSplineCurve PolesCount=2 KnotsCount=2 Degree=1 IsPeriodic=0
    g18: BSplineCurve PolesCount=2 KnotsCount=2 Degree=1 IsPeriodic=0
    g19: BSplineCurve PolesCount=2 KnotsCount=2 Degree=1 IsPeriodic=0
    g20: BSplineCurve PolesCount=2 KnotsCount=2 Degree=1 IsPeriodic=0
    g21: BSplineCurve PolesCount=2 KnotsCount=2 Degree=1 IsPeriodic=0
    g22: BSplineCurve PolesCount=2 KnotsCount=2 Degree=1 IsPeriodic=0
    g23: BSplineCurve PolesCount=2 KnotsCount=2 Degree=1 IsPeriodic=0
    g24: BSplineCurve PolesCount=2 KnotsCount=2 Degree=1 IsPeriodic=0
    g25: BSplineCurve PolesCount=2 KnotsCount=2 Degree=1 IsPeriodic=0
    g26: BSplineCurve PolesCount=2 KnotsCount=2 Degree=1 IsPeriodic=0
    g27: BSplineCurve PolesCount=2 KnotsCount=2 Degree=1 IsPeriodic=0
    g28: BSplineCurve PolesCount=2 KnotsCount=2 Degree=1 IsPeriodic=0
    g29: BSplineCurve PolesCount=4 KnotsCount=2 Degree=3 IsPeriodic=0
    g30: BSplineCurve PolesCount=4 KnotsCount=2 Degree=3 IsPeriodic=0
    g31: BSplineCurve PolesCount=2 KnotsCount=2 Degree=1 IsPeriodic=0
    g32: BSplineCurve PolesCount=4 KnotsCount=2 Degree=3 IsPeriodic=0
    g33: BSplineCurve PolesCount=4 KnotsCount=2 Degree=3 IsPeriodic=0
    g34: BSplineCurve PolesCount=2 KnotsCount=2 Degree=1 IsPeriodic=0
    g35: BSplineCurve PolesCount=2 KnotsCount=2 Degree=1 IsPeriodic=0
    g36: BSplineCurve PolesCount=2 KnotsCount=2 Degree=1 IsPeriodic=0
    g37: BSplineCurve PolesCount=2 KnotsCount=2 Degree=1 IsPeriodic=0
    g38: BSplineCurve PolesCount=2 KnotsCount=2 Degree=1 IsPeriodic=0
    g39: BSplineCurve PolesCount=2 KnotsCount=2 Degree=1 IsPeriodic=0
    g40: BSplineCurve PolesCount=2 KnotsCount=2 Degree=1 IsPeriodic=0
    g41: BSplineCurve PolesCount=2 KnotsCount=2 Degree=1 IsPeriodic=0
    g42: BSplineCurve PolesCount=2 KnotsCount=2 Degree=1 IsPeriodic=0
    g43: BSplineCurve PolesCount=2 KnotsCount=2 Degree=1 IsPeriodic=0
    g44: BSplineCurve PolesCount=2 KnotsCount=2 Degree=1 IsPeriodic=0
    g45: BSplineCurve PolesCount=2 KnotsCount=2 Degree=1 IsPeriodic=0
    g46: BSplineCurve PolesCount=2 KnotsCount=2 Degree=1 IsPeriodic=0
    g47: BSplineCurve PolesCount=2 KnotsCount=2 Degree=1 IsPeriodic=0
    g48: BSplineCurve PolesCount=2 KnotsCount=2 Degree=1 IsPeriodic=0
    g49: BSplineCurve PolesCount=2 KnotsCount=2 Degree=1 IsPeriodic=0
    g50: BSplineCurve PolesCount=2 KnotsCount=2 Degree=1 IsPeriodic=0
    g51: BSplineCurve PolesCount=2 KnotsCount=2 Degree=1 IsPeriodic=0
    g52: BSplineCurve PolesCount=2 KnotsCount=2 Degree=1 IsPeriodic=0
    g53: BSplineCurve PolesCount=2 KnotsCount=2 Degree=1 IsPeriodic=0
    g54: BSplineCurve PolesCount=2 KnotsCount=2 Degree=1 IsPeriodic=0
    g55: BSplineCurve PolesCount=2 KnotsCount=2 Degree=1 IsPeriodic=0
    g56: BSplineCurve PolesCount=2 KnotsCount=2 Degree=1 IsPeriodic=0
    g57: BSplineCurve PolesCount=2 KnotsCount=2 Degree=1 IsPeriodic=0
    g58: BSplineCurve PolesCount=2 KnotsCount=2 Degree=1 IsPeriodic=0
  constraints (59):
    c: Coincident(g0,g1)
    c: Coincident(g1,g2)
    c: Coincident(g2,g3)
    c: Coincident(g3,g4)
    c: Coincident(g4,g5)
    c: Coincident(g5,g6)
    c: Coincident(g6,g7)
    c: Coincident(g7,g8)
    c: Coincident(g8,g9)
    c: Coincident(g9,g10)
    c: Coincident(g10,g11)
    c: Coincident(g11,g12)
    c: Coincident(g12,g13)
    c: Coincident(g13,g14)
    c: Coincident(g14,g15)
    c: Coincident(g15,g16)
    c: Coincident(g16,g17)
    c: Coincident(g17,g18)
    c: Coincident(g18,g19)
    c: Coincident(g19,g20)
    c: Coincident(g20,g21)
    c: Coincident(g21,g22)
    c: Coincident(g22,g23)
    c: Coincident(g23,g24)
    c: Coincident(g24,g25)
    c: Coincident(g25,g26)
    c: Coincident(g26,g27)
    c: Coincident(g27,g28)
    c: Coincident(g28,g29)
    c: Coincident(g29,g30)
    c: Coincident(g30,g31)
    c: Coincident(g31,g32)
    c: Coincident(g32,g33)
    c: Coincident(g33,g34)
    c: Coincident(g34,g35)
    c: Coincident(g35,g36)
    c: Coincident(g36,g0)
    c: Coincident(g37,g38)
    c: Coincident(g38,g39)
    c: Coincident(g39,g37)
    c: Coincident(g40,g41)
    c: Coincident(g41,g42)
    c: Coincident(g42,g43)
    c: Coincident(g43,g44)
    c: Coincident(g44,g45)
    c: Coincident(g45,g46)
    c: Coincident(g46,g47)
    c: Coincident(g47,g40)
    c: Coincident(g48,g49)
    c: Coincident(g49,g50)
    c: Coincident(g50,g48)
    c: Coincident(g51,g52)
    c: Coincident(g52,g53)
    c: Coincident(g53,g54)
    c: Coincident(g54,g55)
    c: Coincident(g55,g56)
    c: Coincident(g56,g57)
    c: Coincident(g57,g58)
    c: Coincident(g58,g51)
FEATURE [PartDesign::Pocket] Pocket018  label="AAMSX Logo Window Pocket"
  BaseFeature = -> Fillet004
  Length = 0.6
  Length2 = 100
  Profile = -> Sketch049
  Reversed = true
  Type = 0
  expr: Length = Spreadsheet001.case_wall_thickness / 2
FEATURE [PartDesign::Pad] Pad010
  BaseFeature = -> Pocket018
  Direction = (1,1,1)
  Length = 0.6
  Length2 = 100
  Profile = -> Sketch050
  Type = 0
  expr: Length = Spreadsheet001.case_wall_thickness / 2
FEATURE [PartDesign::Body] Body002  label="case wired001"
  Group = -> [DatumPlane002,Sketch034,Pad006,Fillet005,Sketch035,Pocket014,Sketch039,Pocket015,Sketch038,Pad008,Sketch037,Hole004,Pocket016,Hole005,Sketch043,Sketch046,MultiTransform002,Pocket013,LinearPattern005,Sketch044,Pocket017,Pocket012,Sketch041,Sketch045,Sketch042,Pad007,Sketch048,Pad009,Fillet004,Sketch047,Sketch040,Sketch036,Sketch049,Pocket018,Sketch050,Pad010]
  Origin = -> Origin011
  Tip = -> Pad010
FEATURE [Part::FeaturePython] Slice002  # WARN: FeaturePython — macro-defined, semantics opaque (R4)
  Base = -> Body002
  Mode = 1
  Tolerance = 0
  Tools = -> [Extrude006,Extrude007,Extrude008]
FEATURE [Part::FeaturePython] Slice001_child002  label="Top wired001"  # WARN: FeaturePython — macro-defined, semantics opaque (R4)
  Base = -> Slice002
  FilterType = 1
  Invert = false
  OverrideMaxVal = 0
  WindowFrom = 80
  WindowTo = 100
  items = 1
FEATURE [Part::FeaturePython] Slice001_child003  label="Bottom wired001"  # WARN: FeaturePython — macro-defined, semantics opaque (R4)
  Base = -> Slice002
  FilterType = 1
  Invert = false
  OverrideMaxVal = 0
  WindowFrom = 80
  WindowTo = 100
  items = 0
FEATURE [App::DocumentObjectGroup] GrExplode_Slice002  label="MSX-Mega Adapter wired AAMSX"
  Group = -> [Slice001_child003,Slice001_child002]
